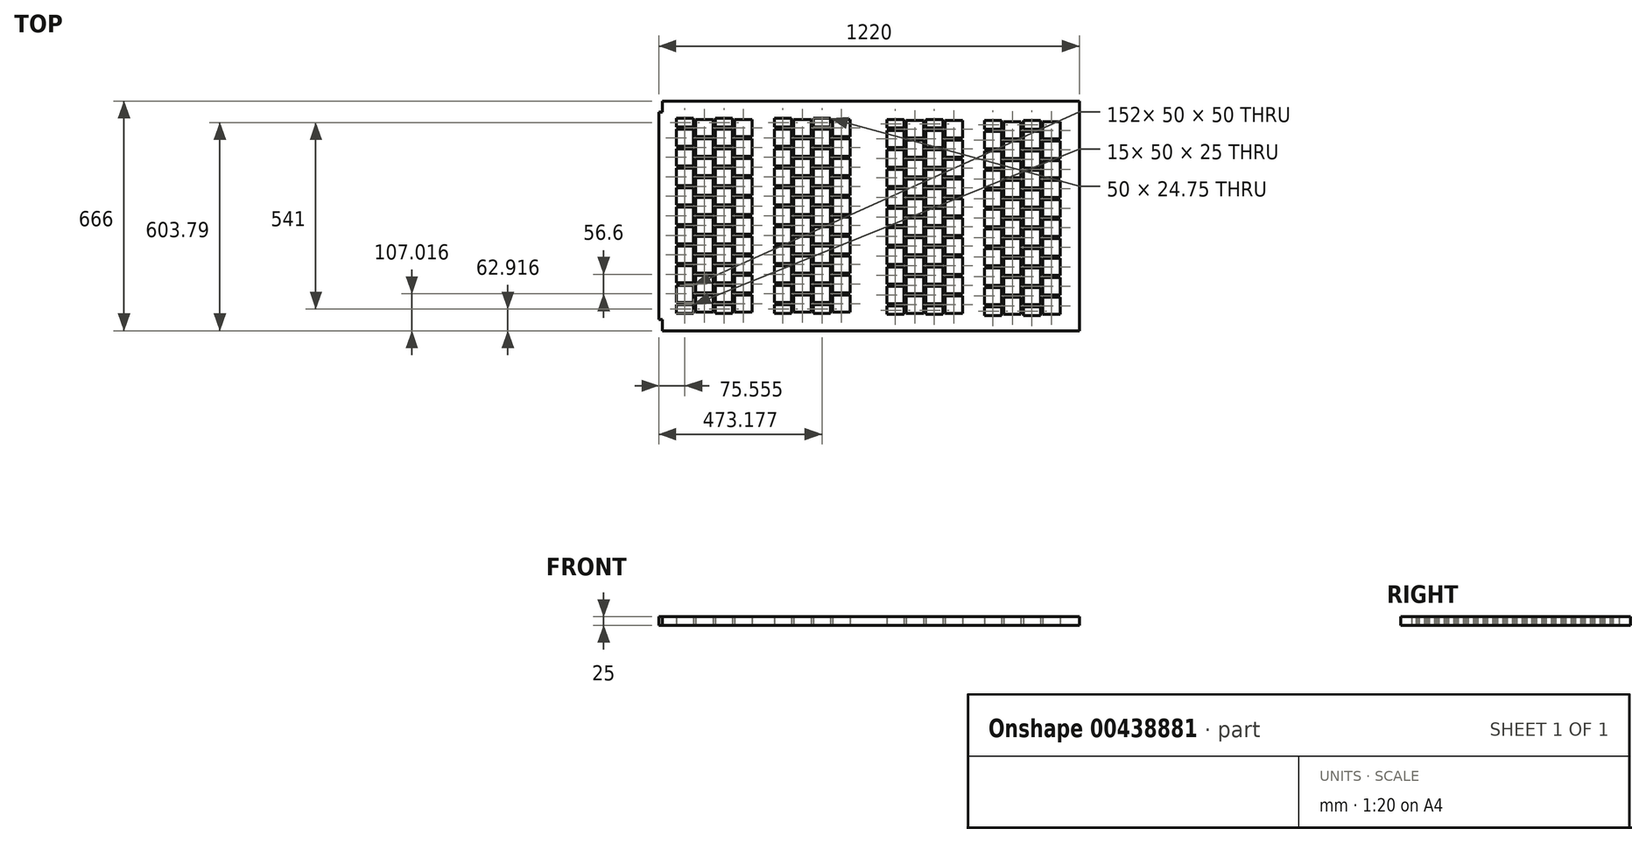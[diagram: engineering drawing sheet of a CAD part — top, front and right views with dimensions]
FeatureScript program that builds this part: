
annotation { "Feature Type Name" : "Feature", "Feature Type Description" : "" }
export const myFeature = defineFeature(function(context is Context, id is Id, definition is map)
    precondition{}
    {
        {
            var Q0;
            Q0=qCreatedBy(makeId("Top.planeOp"),FACE);
            var sketch = newSketch(context, id + "F0", { "sketchPlane" : qUnion([Q0])});
            skLineSegment(sketch, "E0", {"start": v(-1823.33, -56.7) * mm, "end": v(-1823.33, -81.7) * mm});
            skLineSegment(sketch, "E1", {"start": v(-1823.33, -81.7) * mm, "end": v(-1773.33, -81.7) * mm});
            skLineSegment(sketch, "E2", {"start": v(-1773.33, -81.7) * mm, "end": v(-1773.33, -56.7) * mm});
            skLineSegment(sketch, "E3.bottom", {"start": v(-1823.33, -88.3) * mm, "end": v(-1823.33, -138.3) * mm});
            skLineSegment(sketch, "E3.top", {"start": v(-1773.33, -88.3) * mm, "end": v(-1773.33, -138.3) * mm});
            skLineSegment(sketch, "E3.left", {"start": v(-1823.33, -88.3) * mm, "end": v(-1773.33, -88.3) * mm});
            skLineSegment(sketch, "E3.right", {"start": v(-1823.33, -138.3) * mm, "end": v(-1773.33, -138.3) * mm});
            skLineSegment(sketch, "E4.bottom", {"start": v(-1823.33, -144.9) * mm, "end": v(-1823.33, -194.9) * mm});
            skLineSegment(sketch, "E4.top", {"start": v(-1773.33, -144.9) * mm, "end": v(-1773.33, -194.9) * mm});
            skLineSegment(sketch, "E4.left", {"start": v(-1823.33, -144.9) * mm, "end": v(-1773.33, -144.9) * mm});
            skLineSegment(sketch, "E4.right", {"start": v(-1823.33, -194.9) * mm, "end": v(-1773.33, -194.9) * mm});
            skLineSegment(sketch, "E5.bottom", {"start": v(-1823.33, -201.5) * mm, "end": v(-1823.33, -251.5) * mm});
            skLineSegment(sketch, "E5.top", {"start": v(-1773.33, -201.5) * mm, "end": v(-1773.33, -251.5) * mm});
            skLineSegment(sketch, "E5.left", {"start": v(-1823.33, -201.5) * mm, "end": v(-1773.33, -201.5) * mm});
            skLineSegment(sketch, "E5.right", {"start": v(-1823.33, -251.5) * mm, "end": v(-1773.33, -251.5) * mm});
            skLineSegment(sketch, "E6.bottom", {"start": v(-1823.33, -258.1) * mm, "end": v(-1823.33, -308.1) * mm});
            skLineSegment(sketch, "E6.top", {"start": v(-1773.33, -258.1) * mm, "end": v(-1773.33, -308.1) * mm});
            skLineSegment(sketch, "E6.left", {"start": v(-1823.33, -258.1) * mm, "end": v(-1773.33, -258.1) * mm});
            skLineSegment(sketch, "E6.right", {"start": v(-1823.33, -308.1) * mm, "end": v(-1773.33, -308.1) * mm});
            skLineSegment(sketch, "E7.bottom", {"start": v(-1823.33, -314.7) * mm, "end": v(-1823.33, -339.7) * mm});
            skLineSegment(sketch, "E7.top", {"start": v(-1773.33, -314.7) * mm, "end": v(-1773.33, -339.7) * mm});
            skLineSegment(sketch, "E7.left", {"start": v(-1823.33, -314.7) * mm, "end": v(-1773.33, -314.7) * mm});
            skLineSegment(sketch, "E7.right", {"start": v(-1823.33, -339.7) * mm, "end": v(-1773.33, -339.7) * mm});
            skLineSegment(sketch, "E8.bottom", {"start": v(-1766.73, -60) * mm, "end": v(-1766.73, -110) * mm});
            skLineSegment(sketch, "E8.top", {"start": v(-1716.73, -60) * mm, "end": v(-1716.73, -110) * mm});
            skLineSegment(sketch, "E8.left", {"start": v(-1766.73, -60) * mm, "end": v(-1716.73, -60) * mm});
            skLineSegment(sketch, "E8.right", {"start": v(-1766.73, -110) * mm, "end": v(-1716.73, -110) * mm});
            skLineSegment(sketch, "E9.bottom", {"start": v(-1766.73, -116.6) * mm, "end": v(-1766.73, -166.6) * mm});
            skLineSegment(sketch, "E9.top", {"start": v(-1716.73, -116.6) * mm, "end": v(-1716.73, -166.6) * mm});
            skLineSegment(sketch, "E9.left", {"start": v(-1766.73, -116.6) * mm, "end": v(-1716.73, -116.6) * mm});
            skLineSegment(sketch, "E9.right", {"start": v(-1766.73, -166.6) * mm, "end": v(-1716.73, -166.6) * mm});
            skLineSegment(sketch, "E10.bottom", {"start": v(-1766.73, -173.2) * mm, "end": v(-1766.73, -223.2) * mm});
            skLineSegment(sketch, "E10.top", {"start": v(-1716.73, -173.2) * mm, "end": v(-1716.73, -223.2) * mm});
            skLineSegment(sketch, "E10.left", {"start": v(-1766.73, -173.2) * mm, "end": v(-1716.73, -173.2) * mm});
            skLineSegment(sketch, "E10.right", {"start": v(-1766.73, -223.2) * mm, "end": v(-1716.73, -223.2) * mm});
            skLineSegment(sketch, "E11.bottom", {"start": v(-1766.73, -229.8) * mm, "end": v(-1766.73, -279.8) * mm});
            skLineSegment(sketch, "E11.top", {"start": v(-1716.73, -229.8) * mm, "end": v(-1716.73, -279.8) * mm});
            skLineSegment(sketch, "E11.left", {"start": v(-1766.73, -229.8) * mm, "end": v(-1716.73, -229.8) * mm});
            skLineSegment(sketch, "E11.right", {"start": v(-1766.73, -279.8) * mm, "end": v(-1716.73, -279.8) * mm});
            skLineSegment(sketch, "E12.bottom", {"start": v(-1766.73, -286.4) * mm, "end": v(-1766.73, -336.4) * mm});
            skLineSegment(sketch, "E12.top", {"start": v(-1716.73, -286.4) * mm, "end": v(-1716.73, -336.4) * mm});
            skLineSegment(sketch, "E12.left", {"start": v(-1766.73, -286.4) * mm, "end": v(-1716.73, -286.4) * mm});
            skLineSegment(sketch, "E12.right", {"start": v(-1766.73, -336.4) * mm, "end": v(-1716.73, -336.4) * mm});
            skLineSegment(sketch, "E13", {"start": v(-1710.13, -56.7) * mm, "end": v(-1710.13, -81.7) * mm});
            skLineSegment(sketch, "E14", {"start": v(-1710.13, -81.7) * mm, "end": v(-1660.13, -81.7) * mm});
            skLineSegment(sketch, "E15", {"start": v(-1660.13, -81.7) * mm, "end": v(-1660.13, -56.7) * mm});
            skLineSegment(sketch, "E16.bottom", {"start": v(-1710.13, -88.3) * mm, "end": v(-1710.13, -138.3) * mm});
            skLineSegment(sketch, "E16.top", {"start": v(-1660.13, -88.3) * mm, "end": v(-1660.13, -138.3) * mm});
            skLineSegment(sketch, "E16.left", {"start": v(-1710.13, -88.3) * mm, "end": v(-1660.13, -88.3) * mm});
            skLineSegment(sketch, "E16.right", {"start": v(-1710.13, -138.3) * mm, "end": v(-1660.13, -138.3) * mm});
            skLineSegment(sketch, "E17.bottom", {"start": v(-1710.13, -144.9) * mm, "end": v(-1710.13, -194.9) * mm});
            skLineSegment(sketch, "E17.top", {"start": v(-1660.13, -144.9) * mm, "end": v(-1660.13, -194.9) * mm});
            skLineSegment(sketch, "E17.left", {"start": v(-1710.13, -144.9) * mm, "end": v(-1660.13, -144.9) * mm});
            skLineSegment(sketch, "E17.right", {"start": v(-1710.13, -194.9) * mm, "end": v(-1660.13, -194.9) * mm});
            skLineSegment(sketch, "E18.bottom", {"start": v(-1710.13, -201.5) * mm, "end": v(-1710.13, -251.5) * mm});
            skLineSegment(sketch, "E18.top", {"start": v(-1660.13, -201.5) * mm, "end": v(-1660.13, -251.5) * mm});
            skLineSegment(sketch, "E18.left", {"start": v(-1710.13, -201.5) * mm, "end": v(-1660.13, -201.5) * mm});
            skLineSegment(sketch, "E18.right", {"start": v(-1710.13, -251.5) * mm, "end": v(-1660.13, -251.5) * mm});
            skLineSegment(sketch, "E19.bottom", {"start": v(-1710.13, -258.1) * mm, "end": v(-1710.13, -308.1) * mm});
            skLineSegment(sketch, "E19.top", {"start": v(-1660.13, -258.1) * mm, "end": v(-1660.13, -308.1) * mm});
            skLineSegment(sketch, "E19.left", {"start": v(-1710.13, -258.1) * mm, "end": v(-1660.13, -258.1) * mm});
            skLineSegment(sketch, "E19.right", {"start": v(-1710.13, -308.1) * mm, "end": v(-1660.13, -308.1) * mm});
            skLineSegment(sketch, "E20.bottom", {"start": v(-1710.13, -314.7) * mm, "end": v(-1710.13, -339.7) * mm});
            skLineSegment(sketch, "E20.top", {"start": v(-1660.13, -314.7) * mm, "end": v(-1660.13, -339.7) * mm});
            skLineSegment(sketch, "E20.left", {"start": v(-1710.13, -314.7) * mm, "end": v(-1660.13, -314.7) * mm});
            skLineSegment(sketch, "E20.right", {"start": v(-1710.13, -339.7) * mm, "end": v(-1660.13, -339.7) * mm});
            skLineSegment(sketch, "E21.bottom", {"start": v(-1653.53, -60) * mm, "end": v(-1653.53, -110) * mm});
            skLineSegment(sketch, "E21.top", {"start": v(-1603.53, -60) * mm, "end": v(-1603.53, -110) * mm});
            skLineSegment(sketch, "E21.left", {"start": v(-1653.53, -60) * mm, "end": v(-1603.53, -60) * mm});
            skLineSegment(sketch, "E21.right", {"start": v(-1653.53, -110) * mm, "end": v(-1603.53, -110) * mm});
            skLineSegment(sketch, "E22.bottom", {"start": v(-1653.53, -116.6) * mm, "end": v(-1653.53, -166.6) * mm});
            skLineSegment(sketch, "E22.top", {"start": v(-1603.53, -116.6) * mm, "end": v(-1603.53, -166.6) * mm});
            skLineSegment(sketch, "E22.left", {"start": v(-1653.53, -116.6) * mm, "end": v(-1603.53, -116.6) * mm});
            skLineSegment(sketch, "E22.right", {"start": v(-1653.53, -166.6) * mm, "end": v(-1603.53, -166.6) * mm});
            skLineSegment(sketch, "E23.bottom", {"start": v(-1653.53, -173.2) * mm, "end": v(-1653.53, -223.2) * mm});
            skLineSegment(sketch, "E23.top", {"start": v(-1603.53, -173.2) * mm, "end": v(-1603.53, -223.2) * mm});
            skLineSegment(sketch, "E23.left", {"start": v(-1653.53, -173.2) * mm, "end": v(-1603.53, -173.2) * mm});
            skLineSegment(sketch, "E23.right", {"start": v(-1653.53, -223.2) * mm, "end": v(-1603.53, -223.2) * mm});
            skLineSegment(sketch, "E24.bottom", {"start": v(-1653.53, -229.8) * mm, "end": v(-1653.53, -279.8) * mm});
            skLineSegment(sketch, "E24.top", {"start": v(-1603.53, -229.8) * mm, "end": v(-1603.53, -279.8) * mm});
            skLineSegment(sketch, "E24.left", {"start": v(-1653.53, -229.8) * mm, "end": v(-1603.53, -229.8) * mm});
            skLineSegment(sketch, "E24.right", {"start": v(-1653.53, -279.8) * mm, "end": v(-1603.53, -279.8) * mm});
            skLineSegment(sketch, "E25.bottom", {"start": v(-1653.53, -286.4) * mm, "end": v(-1653.53, -336.4) * mm});
            skLineSegment(sketch, "E25.top", {"start": v(-1603.53, -286.4) * mm, "end": v(-1603.53, -336.4) * mm});
            skLineSegment(sketch, "E25.left", {"start": v(-1653.53, -286.4) * mm, "end": v(-1603.53, -286.4) * mm});
            skLineSegment(sketch, "E25.right", {"start": v(-1653.53, -336.4) * mm, "end": v(-1603.53, -336.4) * mm});
            skLineSegment(sketch, "E26.MirrorCS", {"start": v(-1710.13, 201.3) * mm, "end": v(-1660.13, 201.3) * mm});
            skLineSegment(sketch, "E27.MirrorCS", {"start": v(-1653.53, 116.4) * mm, "end": v(-1603.53, 116.4) * mm});
            skLineSegment(sketch, "E28.MirrorCS", {"start": v(-1823.33, 144.7) * mm, "end": v(-1773.33, 144.7) * mm});
            skLineSegment(sketch, "E29.MirrorCS", {"start": v(-1603.53, 3.2) * mm, "end": v(-1603.53, 53.2) * mm});
            skLineSegment(sketch, "E30.MirrorCS", {"start": v(-1716.73, -53.4) * mm, "end": v(-1716.73, -3.4) * mm});
            skLineSegment(sketch, "E31.MirrorCS", {"start": v(-1716.73, 173) * mm, "end": v(-1716.73, 223) * mm});
            skLineSegment(sketch, "E32.MirrorCS", {"start": v(-1660.13, 88.1) * mm, "end": v(-1660.13, 138.1) * mm});
            skLineSegment(sketch, "E33.MirrorCS", {"start": v(-1716.73, 59.8) * mm, "end": v(-1716.73, 109.8) * mm});
            skLineSegment(sketch, "E34.MirrorCS", {"start": v(-1660.13, -25.1) * mm, "end": v(-1660.13, 24.9) * mm});
            skLineSegment(sketch, "E35.MirrorCS", {"start": v(-1660.13, 201.3) * mm, "end": v(-1660.13, 226.3) * mm});
            skLineSegment(sketch, "E36.MirrorCS", {"start": v(-1603.53, 116.4) * mm, "end": v(-1603.53, 166.4) * mm});
            skLineSegment(sketch, "E37.MirrorCS", {"start": v(-1773.33, 144.7) * mm, "end": v(-1773.33, 194.7) * mm});
            skLineSegment(sketch, "E38.MirrorCS", {"start": v(-1653.53, 3.2) * mm, "end": v(-1653.53, 53.2) * mm});
            skLineSegment(sketch, "E39.MirrorCS", {"start": v(-1766.73, 59.8) * mm, "end": v(-1716.73, 59.8) * mm});
            skLineSegment(sketch, "E40.MirrorCS", {"start": v(-1766.73, -53.4) * mm, "end": v(-1766.73, -3.4) * mm});
            skLineSegment(sketch, "E41.MirrorCS", {"start": v(-1766.73, 173) * mm, "end": v(-1766.73, 223) * mm});
            skLineSegment(sketch, "E42.MirrorCS", {"start": v(-1710.13, 88.1) * mm, "end": v(-1710.13, 138.1) * mm});
            skLineSegment(sketch, "E43.MirrorCS", {"start": v(-1766.73, 59.8) * mm, "end": v(-1766.73, 109.8) * mm});
            skLineSegment(sketch, "E44.MirrorCS", {"start": v(-1710.13, -25.1) * mm, "end": v(-1710.13, 24.9) * mm});
            skLineSegment(sketch, "E45.MirrorCS", {"start": v(-1710.13, 201.3) * mm, "end": v(-1710.13, 226.3) * mm});
            skLineSegment(sketch, "E46.MirrorCS", {"start": v(-1653.53, 116.4) * mm, "end": v(-1653.53, 166.4) * mm});
            skLineSegment(sketch, "E47.MirrorCS", {"start": v(-1823.33, 144.7) * mm, "end": v(-1823.33, 194.7) * mm});
            skLineSegment(sketch, "E48.MirrorCS", {"start": v(-1653.53, -3.4) * mm, "end": v(-1603.53, -3.4) * mm});
            skLineSegment(sketch, "E49.MirrorCS", {"start": v(-1653.53, 223) * mm, "end": v(-1603.53, 223) * mm});
            skLineSegment(sketch, "E50.MirrorCS", {"start": v(-1823.33, 226.3) * mm, "end": v(-1773.33, 226.3) * mm});
            skLineSegment(sketch, "E51.MirrorCS", {"start": v(-1766.73, 166.4) * mm, "end": v(-1716.73, 166.4) * mm});
            skLineSegment(sketch, "E52.MirrorCS", {"start": v(-1710.13, 81.5) * mm, "end": v(-1660.13, 81.5) * mm});
            skLineSegment(sketch, "E53.MirrorCS", {"start": v(-1823.33, 88.1) * mm, "end": v(-1823.33, 138.1) * mm});
            skLineSegment(sketch, "E54.MirrorCS", {"start": v(-1823.33, 81.5) * mm, "end": v(-1773.33, 81.5) * mm});
            skLineSegment(sketch, "E55.MirrorCS", {"start": v(-1823.33, 31.5) * mm, "end": v(-1773.33, 31.5) * mm});
            skLineSegment(sketch, "E56.MirrorCS", {"start": v(-1773.33, 31.5) * mm, "end": v(-1773.33, 81.5) * mm});
            skLineSegment(sketch, "E57.MirrorCS", {"start": v(-1823.33, 31.5) * mm, "end": v(-1823.33, 81.5) * mm});
            skLineSegment(sketch, "E58.MirrorCS", {"start": v(-1823.33, 24.9) * mm, "end": v(-1773.33, 24.9) * mm});
            skLineSegment(sketch, "E59.MirrorCS", {"start": v(-1823.33, -25.1) * mm, "end": v(-1773.33, -25.1) * mm});
            skLineSegment(sketch, "E60.MirrorCS", {"start": v(-1773.33, -25.1) * mm, "end": v(-1773.33, 24.9) * mm});
            skLineSegment(sketch, "E61.MirrorCS", {"start": v(-1823.33, -25.1) * mm, "end": v(-1823.33, 24.9) * mm});
            skLineSegment(sketch, "E62.MirrorCS", {"start": v(-1773.33, -31.7) * mm, "end": v(-1773.33, -56.7) * mm});
            skLineSegment(sketch, "E63.MirrorCS", {"start": v(-1823.33, -31.7) * mm, "end": v(-1773.33, -31.7) * mm});
            skLineSegment(sketch, "E64.MirrorCS", {"start": v(-1823.33, -56.7) * mm, "end": v(-1823.33, -31.7) * mm});
            skLineSegment(sketch, "E65.MirrorCS", {"start": v(-1823.33, 138.1) * mm, "end": v(-1773.33, 138.1) * mm});
            skLineSegment(sketch, "E66.MirrorCS", {"start": v(-1823.33, 88.1) * mm, "end": v(-1773.33, 88.1) * mm});
            skLineSegment(sketch, "E67.MirrorCS", {"start": v(-1710.13, -25.1) * mm, "end": v(-1660.13, -25.1) * mm});
            skLineSegment(sketch, "E68.MirrorCS", {"start": v(-1773.33, 88.1) * mm, "end": v(-1773.33, 138.1) * mm});
            skLineSegment(sketch, "E69.MirrorCS", {"start": v(-1766.73, 116.4) * mm, "end": v(-1716.73, 116.4) * mm});
            skLineSegment(sketch, "E70.MirrorCS", {"start": v(-1766.73, 53.2) * mm, "end": v(-1716.73, 53.2) * mm});
            skLineSegment(sketch, "E71.MirrorCS", {"start": v(-1710.13, 31.5) * mm, "end": v(-1660.13, 31.5) * mm});
            skLineSegment(sketch, "E72.MirrorCS", {"start": v(-1660.13, -31.7) * mm, "end": v(-1660.13, -56.7) * mm});
            skLineSegment(sketch, "E73.MirrorCS", {"start": v(-1710.13, 194.7) * mm, "end": v(-1660.13, 194.7) * mm});
            skLineSegment(sketch, "E74.MirrorCS", {"start": v(-1653.53, -53.4) * mm, "end": v(-1603.53, -53.4) * mm});
            skLineSegment(sketch, "E75.MirrorCS", {"start": v(-1653.53, 173) * mm, "end": v(-1603.53, 173) * mm});
            skLineSegment(sketch, "E76.MirrorCS", {"start": v(-1653.53, 109.8) * mm, "end": v(-1603.53, 109.8) * mm});
            skLineSegment(sketch, "E77.MirrorCS", {"start": v(-1823.33, 201.3) * mm, "end": v(-1773.33, 201.3) * mm});
            skLineSegment(sketch, "E78.MirrorCS", {"start": v(-1766.73, 116.4) * mm, "end": v(-1766.73, 166.4) * mm});
            skLineSegment(sketch, "E79.MirrorCS", {"start": v(-1716.73, 3.2) * mm, "end": v(-1716.73, 53.2) * mm});
            skLineSegment(sketch, "E80.MirrorCS", {"start": v(-1710.13, 31.5) * mm, "end": v(-1710.13, 81.5) * mm});
            skLineSegment(sketch, "E81.MirrorCS", {"start": v(-1710.13, 88.1) * mm, "end": v(-1660.13, 88.1) * mm});
            skLineSegment(sketch, "E82.MirrorCS", {"start": v(-1766.73, 173) * mm, "end": v(-1716.73, 173) * mm});
            skLineSegment(sketch, "E83.MirrorCS", {"start": v(-1766.73, 223) * mm, "end": v(-1716.73, 223) * mm});
            skLineSegment(sketch, "E84.MirrorCS", {"start": v(-1710.13, 138.1) * mm, "end": v(-1660.13, 138.1) * mm});
            skLineSegment(sketch, "E85.MirrorCS", {"start": v(-1823.33, 201.3) * mm, "end": v(-1823.33, 226.3) * mm});
            skLineSegment(sketch, "E86.MirrorCS", {"start": v(-1766.73, -53.4) * mm, "end": v(-1716.73, -53.4) * mm});
            skLineSegment(sketch, "E87.MirrorCS", {"start": v(-1716.73, 116.4) * mm, "end": v(-1716.73, 166.4) * mm});
            skLineSegment(sketch, "E88.MirrorCS", {"start": v(-1766.73, 3.2) * mm, "end": v(-1716.73, 3.2) * mm});
            skLineSegment(sketch, "E89.MirrorCS", {"start": v(-1766.73, -3.4) * mm, "end": v(-1716.73, -3.4) * mm});
            skLineSegment(sketch, "E90.MirrorCS", {"start": v(-1653.53, 53.2) * mm, "end": v(-1603.53, 53.2) * mm});
            skLineSegment(sketch, "E91.MirrorCS", {"start": v(-1653.53, 173) * mm, "end": v(-1653.53, 223) * mm});
            skLineSegment(sketch, "E92.MirrorCS", {"start": v(-1603.53, 59.8) * mm, "end": v(-1603.53, 109.8) * mm});
            skLineSegment(sketch, "E93.MirrorCS", {"start": v(-1823.33, 194.7) * mm, "end": v(-1773.33, 194.7) * mm});
            skLineSegment(sketch, "E94.MirrorCS", {"start": v(-1653.53, 166.4) * mm, "end": v(-1603.53, 166.4) * mm});
            skLineSegment(sketch, "E95.MirrorCS", {"start": v(-1766.73, 3.2) * mm, "end": v(-1766.73, 53.2) * mm});
            skLineSegment(sketch, "E96.MirrorCS", {"start": v(-1710.13, 226.3) * mm, "end": v(-1660.13, 226.3) * mm});
            skLineSegment(sketch, "E97.MirrorCS", {"start": v(-1710.13, 144.7) * mm, "end": v(-1710.13, 194.7) * mm});
            skLineSegment(sketch, "E98.MirrorCS", {"start": v(-1653.53, 59.8) * mm, "end": v(-1653.53, 109.8) * mm});
            skLineSegment(sketch, "E99.MirrorCS", {"start": v(-1710.13, -56.7) * mm, "end": v(-1710.13, -31.7) * mm});
            skLineSegment(sketch, "E100.MirrorCS", {"start": v(-1710.13, -31.7) * mm, "end": v(-1660.13, -31.7) * mm});
            skLineSegment(sketch, "E101.MirrorCS", {"start": v(-1660.13, 144.7) * mm, "end": v(-1660.13, 194.7) * mm});
            skLineSegment(sketch, "E102.MirrorCS", {"start": v(-1660.13, 31.5) * mm, "end": v(-1660.13, 81.5) * mm});
            skLineSegment(sketch, "E103.MirrorCS", {"start": v(-1603.53, -53.4) * mm, "end": v(-1603.53, -3.4) * mm});
            skLineSegment(sketch, "E104.MirrorCS", {"start": v(-1766.73, 109.8) * mm, "end": v(-1716.73, 109.8) * mm});
            skLineSegment(sketch, "E105.MirrorCS", {"start": v(-1710.13, 24.9) * mm, "end": v(-1660.13, 24.9) * mm});
            skLineSegment(sketch, "E106.MirrorCS", {"start": v(-1773.33, 201.3) * mm, "end": v(-1773.33, 226.3) * mm});
            skLineSegment(sketch, "E107.MirrorCS", {"start": v(-1653.53, 3.2) * mm, "end": v(-1603.53, 3.2) * mm});
            skLineSegment(sketch, "E108.MirrorCS", {"start": v(-1653.53, 59.8) * mm, "end": v(-1603.53, 59.8) * mm});
            skLineSegment(sketch, "E109.MirrorCS", {"start": v(-1603.53, 173) * mm, "end": v(-1603.53, 223) * mm});
            skLineSegment(sketch, "E110.MirrorCS", {"start": v(-1653.53, -53.4) * mm, "end": v(-1653.53, -3.4) * mm});
            skLineSegment(sketch, "E111.MirrorCS", {"start": v(-1710.13, 144.7) * mm, "end": v(-1660.13, 144.7) * mm});
            skPoint(sketch, "E112.MirrorCS.end.orphan", {"position": v(-1650.16, -56.7) * mm});
            skLineSegment(sketch, "E113", {"start": v(-1538.9, -56.7) * mm, "end": v(-1538.9, -81.7) * mm});
            skLineSegment(sketch, "E114", {"start": v(-1538.9, -81.7) * mm, "end": v(-1488.9, -81.7) * mm});
            skLineSegment(sketch, "E115", {"start": v(-1488.9, -81.7) * mm, "end": v(-1488.9, -56.7) * mm});
            skLineSegment(sketch, "E116.bottom", {"start": v(-1538.9, -88.3) * mm, "end": v(-1538.9, -138.3) * mm});
            skLineSegment(sketch, "E116.top", {"start": v(-1488.9, -88.3) * mm, "end": v(-1488.9, -138.3) * mm});
            skLineSegment(sketch, "E116.left", {"start": v(-1538.9, -88.3) * mm, "end": v(-1488.9, -88.3) * mm});
            skLineSegment(sketch, "E116.right", {"start": v(-1538.9, -138.3) * mm, "end": v(-1488.9, -138.3) * mm});
            skLineSegment(sketch, "E117.bottom", {"start": v(-1538.9, -144.9) * mm, "end": v(-1538.9, -194.9) * mm});
            skLineSegment(sketch, "E117.top", {"start": v(-1488.9, -144.9) * mm, "end": v(-1488.9, -194.9) * mm});
            skLineSegment(sketch, "E117.left", {"start": v(-1538.9, -144.9) * mm, "end": v(-1488.9, -144.9) * mm});
            skLineSegment(sketch, "E117.right", {"start": v(-1538.9, -194.9) * mm, "end": v(-1488.9, -194.9) * mm});
            skLineSegment(sketch, "E118.bottom", {"start": v(-1538.9, -201.5) * mm, "end": v(-1538.9, -251.5) * mm});
            skLineSegment(sketch, "E118.top", {"start": v(-1488.9, -201.5) * mm, "end": v(-1488.9, -251.5) * mm});
            skLineSegment(sketch, "E118.left", {"start": v(-1538.9, -201.5) * mm, "end": v(-1488.9, -201.5) * mm});
            skLineSegment(sketch, "E118.right", {"start": v(-1538.9, -251.5) * mm, "end": v(-1488.9, -251.5) * mm});
            skLineSegment(sketch, "E119.bottom", {"start": v(-1538.9, -258.1) * mm, "end": v(-1538.9, -308.1) * mm});
            skLineSegment(sketch, "E119.top", {"start": v(-1488.9, -258.1) * mm, "end": v(-1488.9, -308.1) * mm});
            skLineSegment(sketch, "E119.left", {"start": v(-1538.9, -258.1) * mm, "end": v(-1488.9, -258.1) * mm});
            skLineSegment(sketch, "E119.right", {"start": v(-1538.9, -308.1) * mm, "end": v(-1488.9, -308.1) * mm});
            skLineSegment(sketch, "E120.bottom", {"start": v(-1538.9, -314.7) * mm, "end": v(-1538.9, -339.7) * mm});
            skLineSegment(sketch, "E120.top", {"start": v(-1488.9, -314.7) * mm, "end": v(-1488.9, -339.7) * mm});
            skLineSegment(sketch, "E120.left", {"start": v(-1538.9, -314.7) * mm, "end": v(-1488.9, -314.7) * mm});
            skLineSegment(sketch, "E120.right", {"start": v(-1538.9, -339.7) * mm, "end": v(-1488.9, -339.7) * mm});
            skLineSegment(sketch, "E121.bottom", {"start": v(-1482.3, -60) * mm, "end": v(-1482.3, -110) * mm});
            skLineSegment(sketch, "E121.top", {"start": v(-1432.3, -60) * mm, "end": v(-1432.3, -110) * mm});
            skLineSegment(sketch, "E121.left", {"start": v(-1482.3, -60) * mm, "end": v(-1432.3, -60) * mm});
            skLineSegment(sketch, "E121.right", {"start": v(-1482.3, -110) * mm, "end": v(-1432.3, -110) * mm});
            skLineSegment(sketch, "E122.bottom", {"start": v(-1482.3, -116.6) * mm, "end": v(-1482.3, -166.6) * mm});
            skLineSegment(sketch, "E122.top", {"start": v(-1432.3, -116.6) * mm, "end": v(-1432.3, -166.6) * mm});
            skLineSegment(sketch, "E122.left", {"start": v(-1482.3, -116.6) * mm, "end": v(-1432.3, -116.6) * mm});
            skLineSegment(sketch, "E122.right", {"start": v(-1482.3, -166.6) * mm, "end": v(-1432.3, -166.6) * mm});
            skLineSegment(sketch, "E123.bottom", {"start": v(-1482.3, -173.2) * mm, "end": v(-1482.3, -223.2) * mm});
            skLineSegment(sketch, "E123.top", {"start": v(-1432.3, -173.2) * mm, "end": v(-1432.3, -223.2) * mm});
            skLineSegment(sketch, "E123.left", {"start": v(-1482.3, -173.2) * mm, "end": v(-1432.3, -173.2) * mm});
            skLineSegment(sketch, "E123.right", {"start": v(-1482.3, -223.2) * mm, "end": v(-1432.3, -223.2) * mm});
            skLineSegment(sketch, "E124.bottom", {"start": v(-1482.3, -229.8) * mm, "end": v(-1482.3, -279.8) * mm});
            skLineSegment(sketch, "E124.top", {"start": v(-1432.3, -229.8) * mm, "end": v(-1432.3, -279.8) * mm});
            skLineSegment(sketch, "E124.left", {"start": v(-1482.3, -229.8) * mm, "end": v(-1432.3, -229.8) * mm});
            skLineSegment(sketch, "E124.right", {"start": v(-1482.3, -279.8) * mm, "end": v(-1432.3, -279.8) * mm});
            skLineSegment(sketch, "E125.bottom", {"start": v(-1482.3, -286.4) * mm, "end": v(-1482.3, -336.4) * mm});
            skLineSegment(sketch, "E125.top", {"start": v(-1432.3, -286.4) * mm, "end": v(-1432.3, -336.4) * mm});
            skLineSegment(sketch, "E125.left", {"start": v(-1482.3, -286.4) * mm, "end": v(-1432.3, -286.4) * mm});
            skLineSegment(sketch, "E125.right", {"start": v(-1482.3, -336.4) * mm, "end": v(-1432.3, -336.4) * mm});
            skLineSegment(sketch, "E126", {"start": v(-1425.7, -56.7) * mm, "end": v(-1425.7, -81.7) * mm});
            skLineSegment(sketch, "E127", {"start": v(-1425.7, -81.7) * mm, "end": v(-1375.7, -81.7) * mm});
            skLineSegment(sketch, "E128", {"start": v(-1375.7, -81.7) * mm, "end": v(-1375.7, -56.7) * mm});
            skLineSegment(sketch, "E129.bottom", {"start": v(-1425.7, -88.3) * mm, "end": v(-1425.7, -138.3) * mm});
            skLineSegment(sketch, "E129.top", {"start": v(-1375.7, -88.3) * mm, "end": v(-1375.7, -138.3) * mm});
            skLineSegment(sketch, "E129.left", {"start": v(-1425.7, -88.3) * mm, "end": v(-1375.7, -88.3) * mm});
            skLineSegment(sketch, "E129.right", {"start": v(-1425.7, -138.3) * mm, "end": v(-1375.7, -138.3) * mm});
            skLineSegment(sketch, "E130.bottom", {"start": v(-1425.7, -144.9) * mm, "end": v(-1425.7, -194.9) * mm});
            skLineSegment(sketch, "E130.top", {"start": v(-1375.7, -144.9) * mm, "end": v(-1375.7, -194.9) * mm});
            skLineSegment(sketch, "E130.left", {"start": v(-1425.7, -144.9) * mm, "end": v(-1375.7, -144.9) * mm});
            skLineSegment(sketch, "E130.right", {"start": v(-1425.7, -194.9) * mm, "end": v(-1375.7, -194.9) * mm});
            skLineSegment(sketch, "E131.bottom", {"start": v(-1425.7, -201.5) * mm, "end": v(-1425.7, -251.5) * mm});
            skLineSegment(sketch, "E131.top", {"start": v(-1375.7, -201.5) * mm, "end": v(-1375.7, -251.5) * mm});
            skLineSegment(sketch, "E131.left", {"start": v(-1425.7, -201.5) * mm, "end": v(-1375.7, -201.5) * mm});
            skLineSegment(sketch, "E131.right", {"start": v(-1425.7, -251.5) * mm, "end": v(-1375.7, -251.5) * mm});
            skLineSegment(sketch, "E132.bottom", {"start": v(-1425.7, -258.1) * mm, "end": v(-1425.7, -308.1) * mm});
            skLineSegment(sketch, "E132.top", {"start": v(-1375.7, -258.1) * mm, "end": v(-1375.7, -308.1) * mm});
            skLineSegment(sketch, "E132.left", {"start": v(-1425.7, -258.1) * mm, "end": v(-1375.7, -258.1) * mm});
            skLineSegment(sketch, "E132.right", {"start": v(-1425.7, -308.1) * mm, "end": v(-1375.7, -308.1) * mm});
            skLineSegment(sketch, "E133.bottom", {"start": v(-1425.7, -314.7) * mm, "end": v(-1425.7, -339.7) * mm});
            skLineSegment(sketch, "E133.top", {"start": v(-1375.7, -314.7) * mm, "end": v(-1375.7, -339.7) * mm});
            skLineSegment(sketch, "E133.left", {"start": v(-1425.7, -314.7) * mm, "end": v(-1375.7, -314.7) * mm});
            skLineSegment(sketch, "E133.right", {"start": v(-1425.7, -339.7) * mm, "end": v(-1375.7, -339.7) * mm});
            skLineSegment(sketch, "E134.bottom", {"start": v(-1369.1, -60) * mm, "end": v(-1369.1, -110) * mm});
            skLineSegment(sketch, "E134.top", {"start": v(-1319.1, -60) * mm, "end": v(-1319.1, -110) * mm});
            skLineSegment(sketch, "E134.left", {"start": v(-1369.1, -60) * mm, "end": v(-1319.1, -60) * mm});
            skLineSegment(sketch, "E134.right", {"start": v(-1369.1, -110) * mm, "end": v(-1319.1, -110) * mm});
            skLineSegment(sketch, "E135.bottom", {"start": v(-1369.1, -116.6) * mm, "end": v(-1369.1, -166.6) * mm});
            skLineSegment(sketch, "E135.top", {"start": v(-1319.1, -116.6) * mm, "end": v(-1319.1, -166.6) * mm});
            skLineSegment(sketch, "E135.left", {"start": v(-1369.1, -116.6) * mm, "end": v(-1319.1, -116.6) * mm});
            skLineSegment(sketch, "E135.right", {"start": v(-1369.1, -166.6) * mm, "end": v(-1319.1, -166.6) * mm});
            skLineSegment(sketch, "E136.bottom", {"start": v(-1369.1, -173.2) * mm, "end": v(-1369.1, -223.2) * mm});
            skLineSegment(sketch, "E136.top", {"start": v(-1319.1, -173.2) * mm, "end": v(-1319.1, -223.2) * mm});
            skLineSegment(sketch, "E136.left", {"start": v(-1369.1, -173.2) * mm, "end": v(-1319.1, -173.2) * mm});
            skLineSegment(sketch, "E136.right", {"start": v(-1369.1, -223.2) * mm, "end": v(-1319.1, -223.2) * mm});
            skLineSegment(sketch, "E137.bottom", {"start": v(-1369.1, -229.8) * mm, "end": v(-1369.1, -279.8) * mm});
            skLineSegment(sketch, "E137.top", {"start": v(-1319.1, -229.8) * mm, "end": v(-1319.1, -279.8) * mm});
            skLineSegment(sketch, "E137.left", {"start": v(-1369.1, -229.8) * mm, "end": v(-1319.1, -229.8) * mm});
            skLineSegment(sketch, "E137.right", {"start": v(-1369.1, -279.8) * mm, "end": v(-1319.1, -279.8) * mm});
            skLineSegment(sketch, "E138.bottom", {"start": v(-1369.1, -286.4) * mm, "end": v(-1369.1, -336.4) * mm});
            skLineSegment(sketch, "E138.top", {"start": v(-1319.1, -286.4) * mm, "end": v(-1319.1, -336.4) * mm});
            skLineSegment(sketch, "E138.left", {"start": v(-1369.1, -286.4) * mm, "end": v(-1319.1, -286.4) * mm});
            skLineSegment(sketch, "E138.right", {"start": v(-1369.1, -336.4) * mm, "end": v(-1319.1, -336.4) * mm});
            skLineSegment(sketch, "E139.MirrorCS", {"start": v(-1425.7, 201.3) * mm, "end": v(-1375.7, 201.3) * mm});
            skLineSegment(sketch, "E140.MirrorCS", {"start": v(-1369.1, 116.4) * mm, "end": v(-1319.1, 116.4) * mm});
            skLineSegment(sketch, "E141.MirrorCS", {"start": v(-1538.9, 144.7) * mm, "end": v(-1488.9, 144.7) * mm});
            skLineSegment(sketch, "E142.MirrorCS", {"start": v(-1319.1, 3.2) * mm, "end": v(-1319.1, 53.2) * mm});
            skLineSegment(sketch, "E143.MirrorCS", {"start": v(-1432.3, -53.4) * mm, "end": v(-1432.3, -3.4) * mm});
            skLineSegment(sketch, "E144.MirrorCS", {"start": v(-1432.3, 173) * mm, "end": v(-1432.3, 223) * mm});
            skLineSegment(sketch, "E145.MirrorCS", {"start": v(-1375.7, 88.1) * mm, "end": v(-1375.7, 138.1) * mm});
            skLineSegment(sketch, "E146.MirrorCS", {"start": v(-1432.3, 59.8) * mm, "end": v(-1432.3, 109.8) * mm});
            skLineSegment(sketch, "E147.MirrorCS", {"start": v(-1375.7, -25.1) * mm, "end": v(-1375.7, 24.9) * mm});
            skLineSegment(sketch, "E148.MirrorCS", {"start": v(-1375.7, 201.3) * mm, "end": v(-1375.7, 226.3) * mm});
            skLineSegment(sketch, "E149.MirrorCS", {"start": v(-1319.1, 116.4) * mm, "end": v(-1319.1, 166.4) * mm});
            skLineSegment(sketch, "E150.MirrorCS", {"start": v(-1488.9, 144.7) * mm, "end": v(-1488.9, 194.7) * mm});
            skLineSegment(sketch, "E151.MirrorCS", {"start": v(-1369.1, 3.2) * mm, "end": v(-1369.1, 53.2) * mm});
            skLineSegment(sketch, "E152.MirrorCS", {"start": v(-1482.3, 59.8) * mm, "end": v(-1432.3, 59.8) * mm});
            skLineSegment(sketch, "E153.MirrorCS", {"start": v(-1482.3, -53.4) * mm, "end": v(-1482.3, -3.4) * mm});
            skLineSegment(sketch, "E154.MirrorCS", {"start": v(-1482.3, 173) * mm, "end": v(-1482.3, 223) * mm});
            skLineSegment(sketch, "E155.MirrorCS", {"start": v(-1425.7, 88.1) * mm, "end": v(-1425.7, 138.1) * mm});
            skLineSegment(sketch, "E156.MirrorCS", {"start": v(-1482.3, 59.8) * mm, "end": v(-1482.3, 109.8) * mm});
            skLineSegment(sketch, "E157.MirrorCS", {"start": v(-1425.7, -25.1) * mm, "end": v(-1425.7, 24.9) * mm});
            skLineSegment(sketch, "E158.MirrorCS", {"start": v(-1425.7, 201.3) * mm, "end": v(-1425.7, 226.3) * mm});
            skLineSegment(sketch, "E159.MirrorCS", {"start": v(-1369.1, 116.4) * mm, "end": v(-1369.1, 166.4) * mm});
            skLineSegment(sketch, "E160.MirrorCS", {"start": v(-1538.9, 144.7) * mm, "end": v(-1538.9, 194.7) * mm});
            skLineSegment(sketch, "E161.MirrorCS", {"start": v(-1369.1, -3.4) * mm, "end": v(-1319.1, -3.4) * mm});
            skLineSegment(sketch, "E162.MirrorCS", {"start": v(-1369.1, 223) * mm, "end": v(-1319.1, 223) * mm});
            skLineSegment(sketch, "E163.MirrorCS", {"start": v(-1482.3, 166.4) * mm, "end": v(-1432.3, 166.4) * mm});
            skLineSegment(sketch, "E164.MirrorCS", {"start": v(-1425.7, 81.5) * mm, "end": v(-1375.7, 81.5) * mm});
            skLineSegment(sketch, "E165.MirrorCS", {"start": v(-1538.9, 88.1) * mm, "end": v(-1538.9, 138.1) * mm});
            skLineSegment(sketch, "E166.MirrorCS", {"start": v(-1538.9, 81.5) * mm, "end": v(-1488.9, 81.5) * mm});
            skLineSegment(sketch, "E167.MirrorCS", {"start": v(-1538.9, 31.5) * mm, "end": v(-1488.9, 31.5) * mm});
            skLineSegment(sketch, "E168.MirrorCS", {"start": v(-1488.9, 31.5) * mm, "end": v(-1488.9, 81.5) * mm});
            skLineSegment(sketch, "E169.MirrorCS", {"start": v(-1538.9, 31.5) * mm, "end": v(-1538.9, 81.5) * mm});
            skLineSegment(sketch, "E170.MirrorCS", {"start": v(-1538.9, 24.9) * mm, "end": v(-1488.9, 24.9) * mm});
            skLineSegment(sketch, "E171.MirrorCS", {"start": v(-1538.9, -25.1) * mm, "end": v(-1488.9, -25.1) * mm});
            skLineSegment(sketch, "E172.MirrorCS", {"start": v(-1488.9, -25.1) * mm, "end": v(-1488.9, 24.9) * mm});
            skLineSegment(sketch, "E173.MirrorCS", {"start": v(-1538.9, -25.1) * mm, "end": v(-1538.9, 24.9) * mm});
            skLineSegment(sketch, "E174.MirrorCS", {"start": v(-1488.9, -31.7) * mm, "end": v(-1488.9, -56.7) * mm});
            skLineSegment(sketch, "E175.MirrorCS", {"start": v(-1538.9, -31.7) * mm, "end": v(-1488.9, -31.7) * mm});
            skLineSegment(sketch, "E176.MirrorCS", {"start": v(-1538.9, -56.7) * mm, "end": v(-1538.9, -31.7) * mm});
            skLineSegment(sketch, "E177.MirrorCS", {"start": v(-1538.9, 138.1) * mm, "end": v(-1488.9, 138.1) * mm});
            skLineSegment(sketch, "E178.MirrorCS", {"start": v(-1538.9, 88.1) * mm, "end": v(-1488.9, 88.1) * mm});
            skLineSegment(sketch, "E179.MirrorCS", {"start": v(-1425.7, -25.1) * mm, "end": v(-1375.7, -25.1) * mm});
            skLineSegment(sketch, "E180.MirrorCS", {"start": v(-1488.9, 88.1) * mm, "end": v(-1488.9, 138.1) * mm});
            skLineSegment(sketch, "E181.MirrorCS", {"start": v(-1482.3, 116.4) * mm, "end": v(-1432.3, 116.4) * mm});
            skLineSegment(sketch, "E182.MirrorCS", {"start": v(-1482.3, 53.2) * mm, "end": v(-1432.3, 53.2) * mm});
            skLineSegment(sketch, "E183.MirrorCS", {"start": v(-1425.7, 31.5) * mm, "end": v(-1375.7, 31.5) * mm});
            skLineSegment(sketch, "E184.MirrorCS", {"start": v(-1375.7, -31.7) * mm, "end": v(-1375.7, -56.7) * mm});
            skLineSegment(sketch, "E185.MirrorCS", {"start": v(-1425.7, 194.7) * mm, "end": v(-1375.7, 194.7) * mm});
            skLineSegment(sketch, "E186.MirrorCS", {"start": v(-1369.1, -53.4) * mm, "end": v(-1319.1, -53.4) * mm});
            skLineSegment(sketch, "E187.MirrorCS", {"start": v(-1369.1, 173) * mm, "end": v(-1319.1, 173) * mm});
            skLineSegment(sketch, "E188.MirrorCS", {"start": v(-1369.1, 109.8) * mm, "end": v(-1319.1, 109.8) * mm});
            skLineSegment(sketch, "E189.MirrorCS", {"start": v(-1538.9, 201.3) * mm, "end": v(-1488.9, 201.3) * mm});
            skLineSegment(sketch, "E190.MirrorCS", {"start": v(-1482.3, 116.4) * mm, "end": v(-1482.3, 166.4) * mm});
            skLineSegment(sketch, "E191.MirrorCS", {"start": v(-1432.3, 3.2) * mm, "end": v(-1432.3, 53.2) * mm});
            skLineSegment(sketch, "E192.MirrorCS", {"start": v(-1425.7, 31.5) * mm, "end": v(-1425.7, 81.5) * mm});
            skLineSegment(sketch, "E193.MirrorCS", {"start": v(-1425.7, 88.1) * mm, "end": v(-1375.7, 88.1) * mm});
            skLineSegment(sketch, "E194.MirrorCS", {"start": v(-1482.3, 173) * mm, "end": v(-1432.3, 173) * mm});
            skLineSegment(sketch, "E195.MirrorCS", {"start": v(-1482.3, 223) * mm, "end": v(-1432.3, 223) * mm});
            skLineSegment(sketch, "E196.MirrorCS", {"start": v(-1425.7, 138.1) * mm, "end": v(-1375.7, 138.1) * mm});
            skLineSegment(sketch, "E197.MirrorCS", {"start": v(-1538.9, 201.3) * mm, "end": v(-1538.9, 226.3) * mm});
            skLineSegment(sketch, "E198.MirrorCS", {"start": v(-1482.3, -53.4) * mm, "end": v(-1432.3, -53.4) * mm});
            skLineSegment(sketch, "E199.MirrorCS", {"start": v(-1432.3, 116.4) * mm, "end": v(-1432.3, 166.4) * mm});
            skLineSegment(sketch, "E200.MirrorCS", {"start": v(-1482.3, 3.2) * mm, "end": v(-1432.3, 3.2) * mm});
            skLineSegment(sketch, "E201.MirrorCS", {"start": v(-1482.3, -3.4) * mm, "end": v(-1432.3, -3.4) * mm});
            skLineSegment(sketch, "E202.MirrorCS", {"start": v(-1369.1, 53.2) * mm, "end": v(-1319.1, 53.2) * mm});
            skLineSegment(sketch, "E203.MirrorCS", {"start": v(-1369.1, 173) * mm, "end": v(-1369.1, 223) * mm});
            skLineSegment(sketch, "E204.MirrorCS", {"start": v(-1319.1, 59.8) * mm, "end": v(-1319.1, 109.8) * mm});
            skLineSegment(sketch, "E205.MirrorCS", {"start": v(-1538.9, 194.7) * mm, "end": v(-1488.9, 194.7) * mm});
            skLineSegment(sketch, "E206.MirrorCS", {"start": v(-1369.1, 166.4) * mm, "end": v(-1319.1, 166.4) * mm});
            skLineSegment(sketch, "E207.MirrorCS", {"start": v(-1482.3, 3.2) * mm, "end": v(-1482.3, 53.2) * mm});
            skLineSegment(sketch, "E208.MirrorCS", {"start": v(-1425.7, 144.7) * mm, "end": v(-1425.7, 194.7) * mm});
            skLineSegment(sketch, "E209.MirrorCS", {"start": v(-1369.1, 59.8) * mm, "end": v(-1369.1, 109.8) * mm});
            skLineSegment(sketch, "E210.MirrorCS", {"start": v(-1425.7, -56.7) * mm, "end": v(-1425.7, -31.7) * mm});
            skLineSegment(sketch, "E211.MirrorCS", {"start": v(-1425.7, -31.7) * mm, "end": v(-1375.7, -31.7) * mm});
            skLineSegment(sketch, "E212.MirrorCS", {"start": v(-1375.7, 144.7) * mm, "end": v(-1375.7, 194.7) * mm});
            skLineSegment(sketch, "E213.MirrorCS", {"start": v(-1375.7, 31.5) * mm, "end": v(-1375.7, 81.5) * mm});
            skLineSegment(sketch, "E214.MirrorCS", {"start": v(-1319.1, -53.4) * mm, "end": v(-1319.1, -3.4) * mm});
            skLineSegment(sketch, "E215.MirrorCS", {"start": v(-1482.3, 109.8) * mm, "end": v(-1432.3, 109.8) * mm});
            skLineSegment(sketch, "E216.MirrorCS", {"start": v(-1425.7, 24.9) * mm, "end": v(-1375.7, 24.9) * mm});
            skLineSegment(sketch, "E217.MirrorCS", {"start": v(-1488.9, 201.3) * mm, "end": v(-1488.9, 226.3) * mm});
            skLineSegment(sketch, "E218.MirrorCS", {"start": v(-1369.1, 3.2) * mm, "end": v(-1319.1, 3.2) * mm});
            skLineSegment(sketch, "E219.MirrorCS", {"start": v(-1369.1, 59.8) * mm, "end": v(-1319.1, 59.8) * mm});
            skLineSegment(sketch, "E220.MirrorCS", {"start": v(-1319.1, 173) * mm, "end": v(-1319.1, 223) * mm});
            skLineSegment(sketch, "E221.MirrorCS", {"start": v(-1369.1, -53.4) * mm, "end": v(-1369.1, -3.4) * mm});
            skLineSegment(sketch, "E222.MirrorCS", {"start": v(-1425.7, 144.7) * mm, "end": v(-1375.7, 144.7) * mm});
            skLineSegment(sketch, "E223", {"start": v(-1538.9, 226.3) * mm, "end": v(-1488.9, 226.18) * mm});
            skLineSegment(sketch, "E224.trimOffspring", {"start": v(-1425.7, 226.04) * mm, "end": v(-1375.7, 225.93) * mm});
            skLineSegment(sketch, "E225", {"start": v(-1212.69, -60) * mm, "end": v(-1212.69, -85) * mm});
            skLineSegment(sketch, "E226", {"start": v(-1212.69, -85) * mm, "end": v(-1162.69, -85) * mm});
            skLineSegment(sketch, "E227", {"start": v(-1162.69, -85) * mm, "end": v(-1162.69, -60) * mm});
            skLineSegment(sketch, "E228.bottom", {"start": v(-1212.69, -91.6) * mm, "end": v(-1212.69, -141.6) * mm});
            skLineSegment(sketch, "E228.top", {"start": v(-1162.69, -91.6) * mm, "end": v(-1162.69, -141.6) * mm});
            skLineSegment(sketch, "E228.left", {"start": v(-1212.69, -91.6) * mm, "end": v(-1162.69, -91.6) * mm});
            skLineSegment(sketch, "E228.right", {"start": v(-1212.69, -141.6) * mm, "end": v(-1162.69, -141.6) * mm});
            skLineSegment(sketch, "E229.bottom", {"start": v(-1212.69, -148.2) * mm, "end": v(-1212.69, -198.2) * mm});
            skLineSegment(sketch, "E229.top", {"start": v(-1162.69, -148.2) * mm, "end": v(-1162.69, -198.2) * mm});
            skLineSegment(sketch, "E229.left", {"start": v(-1212.69, -148.2) * mm, "end": v(-1162.69, -148.2) * mm});
            skLineSegment(sketch, "E229.right", {"start": v(-1212.69, -198.2) * mm, "end": v(-1162.69, -198.2) * mm});
            skLineSegment(sketch, "E230.bottom", {"start": v(-1212.69, -204.8) * mm, "end": v(-1212.69, -254.8) * mm});
            skLineSegment(sketch, "E230.top", {"start": v(-1162.69, -204.8) * mm, "end": v(-1162.69, -254.8) * mm});
            skLineSegment(sketch, "E230.left", {"start": v(-1212.69, -204.8) * mm, "end": v(-1162.69, -204.8) * mm});
            skLineSegment(sketch, "E230.right", {"start": v(-1212.69, -254.8) * mm, "end": v(-1162.69, -254.8) * mm});
            skLineSegment(sketch, "E231.bottom", {"start": v(-1212.69, -261.4) * mm, "end": v(-1212.69, -311.4) * mm});
            skLineSegment(sketch, "E231.top", {"start": v(-1162.69, -261.4) * mm, "end": v(-1162.69, -311.4) * mm});
            skLineSegment(sketch, "E231.left", {"start": v(-1212.69, -261.4) * mm, "end": v(-1162.69, -261.4) * mm});
            skLineSegment(sketch, "E231.right", {"start": v(-1212.69, -311.4) * mm, "end": v(-1162.69, -311.4) * mm});
            skLineSegment(sketch, "E232.bottom", {"start": v(-1212.69, -318) * mm, "end": v(-1212.69, -343) * mm});
            skLineSegment(sketch, "E232.top", {"start": v(-1162.69, -318) * mm, "end": v(-1162.69, -343) * mm});
            skLineSegment(sketch, "E232.left", {"start": v(-1212.69, -318) * mm, "end": v(-1162.69, -318) * mm});
            skLineSegment(sketch, "E232.right", {"start": v(-1212.69, -343) * mm, "end": v(-1162.69, -343) * mm});
            skLineSegment(sketch, "E233.bottom", {"start": v(-1156.09, -63.3) * mm, "end": v(-1156.09, -113.3) * mm});
            skLineSegment(sketch, "E233.top", {"start": v(-1106.09, -63.3) * mm, "end": v(-1106.09, -113.3) * mm});
            skLineSegment(sketch, "E233.left", {"start": v(-1156.09, -63.3) * mm, "end": v(-1106.09, -63.3) * mm});
            skLineSegment(sketch, "E233.right", {"start": v(-1156.09, -113.3) * mm, "end": v(-1106.09, -113.3) * mm});
            skLineSegment(sketch, "E234.bottom", {"start": v(-1156.09, -119.9) * mm, "end": v(-1156.09, -169.9) * mm});
            skLineSegment(sketch, "E234.top", {"start": v(-1106.09, -119.9) * mm, "end": v(-1106.09, -169.9) * mm});
            skLineSegment(sketch, "E234.left", {"start": v(-1156.09, -119.9) * mm, "end": v(-1106.09, -119.9) * mm});
            skLineSegment(sketch, "E234.right", {"start": v(-1156.09, -169.9) * mm, "end": v(-1106.09, -169.9) * mm});
            skLineSegment(sketch, "E235.bottom", {"start": v(-1156.09, -176.5) * mm, "end": v(-1156.09, -226.5) * mm});
            skLineSegment(sketch, "E235.top", {"start": v(-1106.09, -176.5) * mm, "end": v(-1106.09, -226.5) * mm});
            skLineSegment(sketch, "E235.left", {"start": v(-1156.09, -176.5) * mm, "end": v(-1106.09, -176.5) * mm});
            skLineSegment(sketch, "E235.right", {"start": v(-1156.09, -226.5) * mm, "end": v(-1106.09, -226.5) * mm});
            skLineSegment(sketch, "E236.bottom", {"start": v(-1156.09, -233.1) * mm, "end": v(-1156.09, -283.1) * mm});
            skLineSegment(sketch, "E236.top", {"start": v(-1106.09, -233.1) * mm, "end": v(-1106.09, -283.1) * mm});
            skLineSegment(sketch, "E236.left", {"start": v(-1156.09, -233.1) * mm, "end": v(-1106.09, -233.1) * mm});
            skLineSegment(sketch, "E236.right", {"start": v(-1156.09, -283.1) * mm, "end": v(-1106.09, -283.1) * mm});
            skLineSegment(sketch, "E237.bottom", {"start": v(-1156.09, -289.7) * mm, "end": v(-1156.09, -339.7) * mm});
            skLineSegment(sketch, "E237.top", {"start": v(-1106.09, -289.7) * mm, "end": v(-1106.09, -339.7) * mm});
            skLineSegment(sketch, "E237.left", {"start": v(-1156.09, -289.7) * mm, "end": v(-1106.09, -289.7) * mm});
            skLineSegment(sketch, "E237.right", {"start": v(-1156.09, -339.7) * mm, "end": v(-1106.09, -339.7) * mm});
            skLineSegment(sketch, "E238", {"start": v(-1099.49, -60) * mm, "end": v(-1099.49, -85) * mm});
            skLineSegment(sketch, "E239", {"start": v(-1099.49, -85) * mm, "end": v(-1049.49, -85) * mm});
            skLineSegment(sketch, "E240", {"start": v(-1049.49, -85) * mm, "end": v(-1049.49, -60) * mm});
            skLineSegment(sketch, "E241.bottom", {"start": v(-1099.49, -91.6) * mm, "end": v(-1099.49, -141.6) * mm});
            skLineSegment(sketch, "E241.top", {"start": v(-1049.49, -91.6) * mm, "end": v(-1049.49, -141.6) * mm});
            skLineSegment(sketch, "E241.left", {"start": v(-1099.49, -91.6) * mm, "end": v(-1049.49, -91.6) * mm});
            skLineSegment(sketch, "E241.right", {"start": v(-1099.49, -141.6) * mm, "end": v(-1049.49, -141.6) * mm});
            skLineSegment(sketch, "E242.bottom", {"start": v(-1099.49, -148.2) * mm, "end": v(-1099.49, -198.2) * mm});
            skLineSegment(sketch, "E242.top", {"start": v(-1049.49, -148.2) * mm, "end": v(-1049.49, -198.2) * mm});
            skLineSegment(sketch, "E242.left", {"start": v(-1099.49, -148.2) * mm, "end": v(-1049.49, -148.2) * mm});
            skLineSegment(sketch, "E242.right", {"start": v(-1099.49, -198.2) * mm, "end": v(-1049.49, -198.2) * mm});
            skLineSegment(sketch, "E243.bottom", {"start": v(-1099.49, -204.8) * mm, "end": v(-1099.49, -254.8) * mm});
            skLineSegment(sketch, "E243.top", {"start": v(-1049.49, -204.8) * mm, "end": v(-1049.49, -254.8) * mm});
            skLineSegment(sketch, "E243.left", {"start": v(-1099.49, -204.8) * mm, "end": v(-1049.49, -204.8) * mm});
            skLineSegment(sketch, "E243.right", {"start": v(-1099.49, -254.8) * mm, "end": v(-1049.49, -254.8) * mm});
            skLineSegment(sketch, "E244.bottom", {"start": v(-1099.49, -261.4) * mm, "end": v(-1099.49, -311.4) * mm});
            skLineSegment(sketch, "E244.top", {"start": v(-1049.49, -261.4) * mm, "end": v(-1049.49, -311.4) * mm});
            skLineSegment(sketch, "E244.left", {"start": v(-1099.49, -261.4) * mm, "end": v(-1049.49, -261.4) * mm});
            skLineSegment(sketch, "E244.right", {"start": v(-1099.49, -311.4) * mm, "end": v(-1049.49, -311.4) * mm});
            skLineSegment(sketch, "E245.bottom", {"start": v(-1099.49, -318) * mm, "end": v(-1099.49, -343) * mm});
            skLineSegment(sketch, "E245.top", {"start": v(-1049.49, -318) * mm, "end": v(-1049.49, -343) * mm});
            skLineSegment(sketch, "E245.left", {"start": v(-1099.49, -318) * mm, "end": v(-1049.49, -318) * mm});
            skLineSegment(sketch, "E245.right", {"start": v(-1099.49, -343) * mm, "end": v(-1049.49, -343) * mm});
            skLineSegment(sketch, "E246.bottom", {"start": v(-1042.89, -63.3) * mm, "end": v(-1042.89, -113.3) * mm});
            skLineSegment(sketch, "E246.top", {"start": v(-992.89, -63.3) * mm, "end": v(-992.89, -113.3) * mm});
            skLineSegment(sketch, "E246.left", {"start": v(-1042.89, -63.3) * mm, "end": v(-992.89, -63.3) * mm});
            skLineSegment(sketch, "E246.right", {"start": v(-1042.89, -113.3) * mm, "end": v(-992.89, -113.3) * mm});
            skLineSegment(sketch, "E247.bottom", {"start": v(-1042.89, -119.9) * mm, "end": v(-1042.89, -169.9) * mm});
            skLineSegment(sketch, "E247.top", {"start": v(-992.89, -119.9) * mm, "end": v(-992.89, -169.9) * mm});
            skLineSegment(sketch, "E247.left", {"start": v(-1042.89, -119.9) * mm, "end": v(-992.89, -119.9) * mm});
            skLineSegment(sketch, "E247.right", {"start": v(-1042.89, -169.9) * mm, "end": v(-992.89, -169.9) * mm});
            skLineSegment(sketch, "E248.bottom", {"start": v(-1042.89, -176.5) * mm, "end": v(-1042.89, -226.5) * mm});
            skLineSegment(sketch, "E248.top", {"start": v(-992.89, -176.5) * mm, "end": v(-992.89, -226.5) * mm});
            skLineSegment(sketch, "E248.left", {"start": v(-1042.89, -176.5) * mm, "end": v(-992.89, -176.5) * mm});
            skLineSegment(sketch, "E248.right", {"start": v(-1042.89, -226.5) * mm, "end": v(-992.89, -226.5) * mm});
            skLineSegment(sketch, "E249.bottom", {"start": v(-1042.89, -233.1) * mm, "end": v(-1042.89, -283.1) * mm});
            skLineSegment(sketch, "E249.top", {"start": v(-992.89, -233.1) * mm, "end": v(-992.89, -283.1) * mm});
            skLineSegment(sketch, "E249.left", {"start": v(-1042.89, -233.1) * mm, "end": v(-992.89, -233.1) * mm});
            skLineSegment(sketch, "E249.right", {"start": v(-1042.89, -283.1) * mm, "end": v(-992.89, -283.1) * mm});
            skLineSegment(sketch, "E250.bottom", {"start": v(-1042.89, -289.7) * mm, "end": v(-1042.89, -339.7) * mm});
            skLineSegment(sketch, "E250.top", {"start": v(-992.89, -289.7) * mm, "end": v(-992.89, -339.7) * mm});
            skLineSegment(sketch, "E250.left", {"start": v(-1042.89, -289.7) * mm, "end": v(-992.89, -289.7) * mm});
            skLineSegment(sketch, "E250.right", {"start": v(-1042.89, -339.7) * mm, "end": v(-992.89, -339.7) * mm});
            skLineSegment(sketch, "E251.MirrorCS", {"start": v(-1099.49, 198) * mm, "end": v(-1049.49, 198) * mm});
            skLineSegment(sketch, "E252.MirrorCS", {"start": v(-1042.89, 113.1) * mm, "end": v(-992.89, 113.1) * mm});
            skLineSegment(sketch, "E253.MirrorCS", {"start": v(-1212.69, 141.4) * mm, "end": v(-1162.69, 141.4) * mm});
            skLineSegment(sketch, "E254.MirrorCS", {"start": v(-992.89, -0.1) * mm, "end": v(-992.89, 49.9) * mm});
            skLineSegment(sketch, "E255.MirrorCS", {"start": v(-1106.09, -56.7) * mm, "end": v(-1106.09, -6.7) * mm});
            skLineSegment(sketch, "E256.MirrorCS", {"start": v(-1106.09, 169.7) * mm, "end": v(-1106.09, 219.7) * mm});
            skLineSegment(sketch, "E257.MirrorCS", {"start": v(-1049.49, 84.8) * mm, "end": v(-1049.49, 134.8) * mm});
            skLineSegment(sketch, "E258.MirrorCS", {"start": v(-1106.09, 56.5) * mm, "end": v(-1106.09, 106.5) * mm});
            skLineSegment(sketch, "E259.MirrorCS", {"start": v(-1049.49, -28.4) * mm, "end": v(-1049.49, 21.6) * mm});
            skLineSegment(sketch, "E260.MirrorCS", {"start": v(-1049.49, 198) * mm, "end": v(-1049.49, 223) * mm});
            skLineSegment(sketch, "E261.MirrorCS", {"start": v(-992.89, 113.1) * mm, "end": v(-992.89, 163.1) * mm});
            skLineSegment(sketch, "E262.MirrorCS", {"start": v(-1162.69, 141.4) * mm, "end": v(-1162.69, 191.4) * mm});
            skLineSegment(sketch, "E263.MirrorCS", {"start": v(-1042.89, -0.1) * mm, "end": v(-1042.89, 49.9) * mm});
            skLineSegment(sketch, "E264.MirrorCS", {"start": v(-1156.09, 56.5) * mm, "end": v(-1106.09, 56.5) * mm});
            skLineSegment(sketch, "E265.MirrorCS", {"start": v(-1156.09, -56.7) * mm, "end": v(-1156.09, -6.7) * mm});
            skLineSegment(sketch, "E266.MirrorCS", {"start": v(-1156.09, 169.7) * mm, "end": v(-1156.09, 219.7) * mm});
            skLineSegment(sketch, "E267.MirrorCS", {"start": v(-1099.49, 84.8) * mm, "end": v(-1099.49, 134.8) * mm});
            skLineSegment(sketch, "E268.MirrorCS", {"start": v(-1156.09, 56.5) * mm, "end": v(-1156.09, 106.5) * mm});
            skLineSegment(sketch, "E269.MirrorCS", {"start": v(-1099.49, -28.4) * mm, "end": v(-1099.49, 21.6) * mm});
            skLineSegment(sketch, "E270.MirrorCS", {"start": v(-1099.49, 198) * mm, "end": v(-1099.49, 223) * mm});
            skLineSegment(sketch, "E271.MirrorCS", {"start": v(-1042.89, 113.1) * mm, "end": v(-1042.89, 163.1) * mm});
            skLineSegment(sketch, "E272.MirrorCS", {"start": v(-1212.69, 141.4) * mm, "end": v(-1212.69, 191.4) * mm});
            skLineSegment(sketch, "E273.MirrorCS", {"start": v(-1042.89, -6.7) * mm, "end": v(-992.89, -6.7) * mm});
            skLineSegment(sketch, "E274.MirrorCS", {"start": v(-1042.89, 219.7) * mm, "end": v(-992.89, 219.7) * mm});
            skLineSegment(sketch, "E275.MirrorCS", {"start": v(-1156.09, 163.1) * mm, "end": v(-1106.09, 163.1) * mm});
            skLineSegment(sketch, "E276.MirrorCS", {"start": v(-1099.49, 78.2) * mm, "end": v(-1049.49, 78.2) * mm});
            skLineSegment(sketch, "E277.MirrorCS", {"start": v(-1212.69, 84.8) * mm, "end": v(-1212.69, 134.8) * mm});
            skLineSegment(sketch, "E278.MirrorCS", {"start": v(-1212.69, 78.2) * mm, "end": v(-1162.69, 78.2) * mm});
            skLineSegment(sketch, "E279.MirrorCS", {"start": v(-1212.69, 28.2) * mm, "end": v(-1162.69, 28.2) * mm});
            skLineSegment(sketch, "E280.MirrorCS", {"start": v(-1162.69, 28.2) * mm, "end": v(-1162.69, 78.2) * mm});
            skLineSegment(sketch, "E281.MirrorCS", {"start": v(-1212.69, 28.2) * mm, "end": v(-1212.69, 78.2) * mm});
            skLineSegment(sketch, "E282.MirrorCS", {"start": v(-1212.69, 21.6) * mm, "end": v(-1162.69, 21.6) * mm});
            skLineSegment(sketch, "E283.MirrorCS", {"start": v(-1212.69, -28.4) * mm, "end": v(-1162.69, -28.4) * mm});
            skLineSegment(sketch, "E284.MirrorCS", {"start": v(-1162.69, -28.4) * mm, "end": v(-1162.69, 21.6) * mm});
            skLineSegment(sketch, "E285.MirrorCS", {"start": v(-1212.69, -28.4) * mm, "end": v(-1212.69, 21.6) * mm});
            skLineSegment(sketch, "E286.MirrorCS", {"start": v(-1162.69, -35) * mm, "end": v(-1162.69, -60) * mm});
            skLineSegment(sketch, "E287.MirrorCS", {"start": v(-1212.69, -35) * mm, "end": v(-1162.69, -35) * mm});
            skLineSegment(sketch, "E288.MirrorCS", {"start": v(-1212.69, -60) * mm, "end": v(-1212.69, -35) * mm});
            skLineSegment(sketch, "E289.MirrorCS", {"start": v(-1212.69, 134.8) * mm, "end": v(-1162.69, 134.8) * mm});
            skLineSegment(sketch, "E290.MirrorCS", {"start": v(-1212.69, 84.8) * mm, "end": v(-1162.69, 84.8) * mm});
            skLineSegment(sketch, "E291.MirrorCS", {"start": v(-1099.49, -28.4) * mm, "end": v(-1049.49, -28.4) * mm});
            skLineSegment(sketch, "E292.MirrorCS", {"start": v(-1162.69, 84.8) * mm, "end": v(-1162.69, 134.8) * mm});
            skLineSegment(sketch, "E293.MirrorCS", {"start": v(-1156.09, 113.1) * mm, "end": v(-1106.09, 113.1) * mm});
            skLineSegment(sketch, "E294.MirrorCS", {"start": v(-1156.09, 49.9) * mm, "end": v(-1106.09, 49.9) * mm});
            skLineSegment(sketch, "E295.MirrorCS", {"start": v(-1099.49, 28.2) * mm, "end": v(-1049.49, 28.2) * mm});
            skLineSegment(sketch, "E296.MirrorCS", {"start": v(-1049.49, -35) * mm, "end": v(-1049.49, -60) * mm});
            skLineSegment(sketch, "E297.MirrorCS", {"start": v(-1099.49, 191.4) * mm, "end": v(-1049.49, 191.4) * mm});
            skLineSegment(sketch, "E298.MirrorCS", {"start": v(-1042.89, -56.7) * mm, "end": v(-992.89, -56.7) * mm});
            skLineSegment(sketch, "E299.MirrorCS", {"start": v(-1042.89, 169.7) * mm, "end": v(-992.89, 169.7) * mm});
            skLineSegment(sketch, "E300.MirrorCS", {"start": v(-1042.89, 106.5) * mm, "end": v(-992.89, 106.5) * mm});
            skLineSegment(sketch, "E301.MirrorCS", {"start": v(-1212.69, 198) * mm, "end": v(-1162.69, 198) * mm});
            skLineSegment(sketch, "E302.MirrorCS", {"start": v(-1156.09, 113.1) * mm, "end": v(-1156.09, 163.1) * mm});
            skLineSegment(sketch, "E303.MirrorCS", {"start": v(-1106.09, -0.1) * mm, "end": v(-1106.09, 49.9) * mm});
            skLineSegment(sketch, "E304.MirrorCS", {"start": v(-1099.49, 28.2) * mm, "end": v(-1099.49, 78.2) * mm});
            skLineSegment(sketch, "E305.MirrorCS", {"start": v(-1099.49, 84.8) * mm, "end": v(-1049.49, 84.8) * mm});
            skLineSegment(sketch, "E306.MirrorCS", {"start": v(-1156.09, 169.7) * mm, "end": v(-1106.09, 169.7) * mm});
            skLineSegment(sketch, "E307.MirrorCS", {"start": v(-1156.09, 219.7) * mm, "end": v(-1106.09, 219.7) * mm});
            skLineSegment(sketch, "E308.MirrorCS", {"start": v(-1099.49, 134.8) * mm, "end": v(-1049.49, 134.8) * mm});
            skLineSegment(sketch, "E309.MirrorCS", {"start": v(-1212.69, 198) * mm, "end": v(-1212.69, 223) * mm});
            skLineSegment(sketch, "E310.MirrorCS", {"start": v(-1156.09, -56.7) * mm, "end": v(-1106.09, -56.7) * mm});
            skLineSegment(sketch, "E311.MirrorCS", {"start": v(-1106.09, 113.1) * mm, "end": v(-1106.09, 163.1) * mm});
            skLineSegment(sketch, "E312.MirrorCS", {"start": v(-1156.09, -0.1) * mm, "end": v(-1106.09, -0.1) * mm});
            skLineSegment(sketch, "E313.MirrorCS", {"start": v(-1156.09, -6.7) * mm, "end": v(-1106.09, -6.7) * mm});
            skLineSegment(sketch, "E314.MirrorCS", {"start": v(-1042.89, 49.9) * mm, "end": v(-992.89, 49.9) * mm});
            skLineSegment(sketch, "E315.MirrorCS", {"start": v(-1042.89, 169.7) * mm, "end": v(-1042.89, 219.7) * mm});
            skLineSegment(sketch, "E316.MirrorCS", {"start": v(-992.89, 56.5) * mm, "end": v(-992.89, 106.5) * mm});
            skLineSegment(sketch, "E317.MirrorCS", {"start": v(-1212.69, 191.4) * mm, "end": v(-1162.69, 191.4) * mm});
            skLineSegment(sketch, "E318.MirrorCS", {"start": v(-1042.89, 163.1) * mm, "end": v(-992.89, 163.1) * mm});
            skLineSegment(sketch, "E319.MirrorCS", {"start": v(-1156.09, -0.1) * mm, "end": v(-1156.09, 49.9) * mm});
            skLineSegment(sketch, "E320.MirrorCS", {"start": v(-1099.49, 223) * mm, "end": v(-1049.49, 223) * mm});
            skLineSegment(sketch, "E321.MirrorCS", {"start": v(-1099.49, 141.4) * mm, "end": v(-1099.49, 191.4) * mm});
            skLineSegment(sketch, "E322.MirrorCS", {"start": v(-1042.89, 56.5) * mm, "end": v(-1042.89, 106.5) * mm});
            skLineSegment(sketch, "E323.MirrorCS", {"start": v(-1099.49, -60) * mm, "end": v(-1099.49, -35) * mm});
            skLineSegment(sketch, "E324.MirrorCS", {"start": v(-1099.49, -35) * mm, "end": v(-1049.49, -35) * mm});
            skLineSegment(sketch, "E325.MirrorCS", {"start": v(-1049.49, 141.4) * mm, "end": v(-1049.49, 191.4) * mm});
            skLineSegment(sketch, "E326.MirrorCS", {"start": v(-1049.49, 28.2) * mm, "end": v(-1049.49, 78.2) * mm});
            skLineSegment(sketch, "E327.MirrorCS", {"start": v(-992.89, -56.7) * mm, "end": v(-992.89, -6.7) * mm});
            skLineSegment(sketch, "E328.MirrorCS", {"start": v(-1156.09, 106.5) * mm, "end": v(-1106.09, 106.5) * mm});
            skLineSegment(sketch, "E329.MirrorCS", {"start": v(-1099.49, 21.6) * mm, "end": v(-1049.49, 21.6) * mm});
            skLineSegment(sketch, "E330.MirrorCS", {"start": v(-1162.69, 198) * mm, "end": v(-1162.69, 223) * mm});
            skLineSegment(sketch, "E331.MirrorCS", {"start": v(-1042.89, -0.1) * mm, "end": v(-992.89, -0.1) * mm});
            skLineSegment(sketch, "E332.MirrorCS", {"start": v(-1042.89, 56.5) * mm, "end": v(-992.89, 56.5) * mm});
            skLineSegment(sketch, "E333.MirrorCS", {"start": v(-992.89, 169.7) * mm, "end": v(-992.89, 219.7) * mm});
            skLineSegment(sketch, "E334.MirrorCS", {"start": v(-1042.89, -56.7) * mm, "end": v(-1042.89, -6.7) * mm});
            skLineSegment(sketch, "E335.MirrorCS", {"start": v(-1099.49, 141.4) * mm, "end": v(-1049.49, 141.4) * mm});
            skPoint(sketch, "E336.end.orphan", {"position": v(-1039.52, -60) * mm});
            skLineSegment(sketch, "E337", {"start": v(-1212.69, 223) * mm, "end": v(-1162.69, 222.88) * mm});
            skLineSegment(sketch, "E338", {"start": v(-929.6, -63.3) * mm, "end": v(-929.6, -88.3) * mm});
            skLineSegment(sketch, "E339", {"start": v(-929.6, -88.3) * mm, "end": v(-879.6, -88.3) * mm});
            skLineSegment(sketch, "E340", {"start": v(-879.6, -88.3) * mm, "end": v(-879.6, -63.3) * mm});
            skLineSegment(sketch, "E341.bottom", {"start": v(-929.6, -94.9) * mm, "end": v(-929.6, -144.9) * mm});
            skLineSegment(sketch, "E341.top", {"start": v(-879.6, -94.9) * mm, "end": v(-879.6, -144.9) * mm});
            skLineSegment(sketch, "E341.left", {"start": v(-929.6, -94.9) * mm, "end": v(-879.6, -94.9) * mm});
            skLineSegment(sketch, "E341.right", {"start": v(-929.6, -144.9) * mm, "end": v(-879.6, -144.9) * mm});
            skLineSegment(sketch, "E342.bottom", {"start": v(-929.6, -151.5) * mm, "end": v(-929.6, -201.5) * mm});
            skLineSegment(sketch, "E342.top", {"start": v(-879.6, -151.5) * mm, "end": v(-879.6, -201.5) * mm});
            skLineSegment(sketch, "E342.left", {"start": v(-929.6, -151.5) * mm, "end": v(-879.6, -151.5) * mm});
            skLineSegment(sketch, "E342.right", {"start": v(-929.6, -201.5) * mm, "end": v(-879.6, -201.5) * mm});
            skLineSegment(sketch, "E343.bottom", {"start": v(-929.6, -208.1) * mm, "end": v(-929.6, -258.1) * mm});
            skLineSegment(sketch, "E343.top", {"start": v(-879.6, -208.1) * mm, "end": v(-879.6, -258.1) * mm});
            skLineSegment(sketch, "E343.left", {"start": v(-929.6, -208.1) * mm, "end": v(-879.6, -208.1) * mm});
            skLineSegment(sketch, "E343.right", {"start": v(-929.6, -258.1) * mm, "end": v(-879.6, -258.1) * mm});
            skLineSegment(sketch, "E344.bottom", {"start": v(-929.6, -264.7) * mm, "end": v(-929.6, -314.7) * mm});
            skLineSegment(sketch, "E344.top", {"start": v(-879.6, -264.7) * mm, "end": v(-879.6, -314.7) * mm});
            skLineSegment(sketch, "E344.left", {"start": v(-929.6, -264.7) * mm, "end": v(-879.6, -264.7) * mm});
            skLineSegment(sketch, "E344.right", {"start": v(-929.6, -314.7) * mm, "end": v(-879.6, -314.7) * mm});
            skLineSegment(sketch, "E345.bottom", {"start": v(-929.6, -321.3) * mm, "end": v(-929.6, -346.3) * mm});
            skLineSegment(sketch, "E345.top", {"start": v(-879.6, -321.3) * mm, "end": v(-879.6, -346.3) * mm});
            skLineSegment(sketch, "E345.left", {"start": v(-929.6, -321.3) * mm, "end": v(-879.6, -321.3) * mm});
            skLineSegment(sketch, "E345.right", {"start": v(-929.6, -346.3) * mm, "end": v(-879.6, -346.3) * mm});
            skLineSegment(sketch, "E346.bottom", {"start": v(-873, -66.6) * mm, "end": v(-873, -116.6) * mm});
            skLineSegment(sketch, "E346.top", {"start": v(-823, -66.6) * mm, "end": v(-823, -116.6) * mm});
            skLineSegment(sketch, "E346.left", {"start": v(-873, -66.6) * mm, "end": v(-823, -66.6) * mm});
            skLineSegment(sketch, "E346.right", {"start": v(-873, -116.6) * mm, "end": v(-823, -116.6) * mm});
            skLineSegment(sketch, "E347.bottom", {"start": v(-873, -123.2) * mm, "end": v(-873, -173.2) * mm});
            skLineSegment(sketch, "E347.top", {"start": v(-823, -123.2) * mm, "end": v(-823, -173.2) * mm});
            skLineSegment(sketch, "E347.left", {"start": v(-873, -123.2) * mm, "end": v(-823, -123.2) * mm});
            skLineSegment(sketch, "E347.right", {"start": v(-873, -173.2) * mm, "end": v(-823, -173.2) * mm});
            skLineSegment(sketch, "E348.bottom", {"start": v(-873, -179.8) * mm, "end": v(-873, -229.8) * mm});
            skLineSegment(sketch, "E348.top", {"start": v(-823, -179.8) * mm, "end": v(-823, -229.8) * mm});
            skLineSegment(sketch, "E348.left", {"start": v(-873, -179.8) * mm, "end": v(-823, -179.8) * mm});
            skLineSegment(sketch, "E348.right", {"start": v(-873, -229.8) * mm, "end": v(-823, -229.8) * mm});
            skLineSegment(sketch, "E349.bottom", {"start": v(-873, -236.4) * mm, "end": v(-873, -286.4) * mm});
            skLineSegment(sketch, "E349.top", {"start": v(-823, -236.4) * mm, "end": v(-823, -286.4) * mm});
            skLineSegment(sketch, "E349.left", {"start": v(-873, -236.4) * mm, "end": v(-823, -236.4) * mm});
            skLineSegment(sketch, "E349.right", {"start": v(-873, -286.4) * mm, "end": v(-823, -286.4) * mm});
            skLineSegment(sketch, "E350.bottom", {"start": v(-873, -293) * mm, "end": v(-873, -343) * mm});
            skLineSegment(sketch, "E350.top", {"start": v(-823, -293) * mm, "end": v(-823, -343) * mm});
            skLineSegment(sketch, "E350.left", {"start": v(-873, -293) * mm, "end": v(-823, -293) * mm});
            skLineSegment(sketch, "E350.right", {"start": v(-873, -343) * mm, "end": v(-823, -343) * mm});
            skLineSegment(sketch, "E351", {"start": v(-816.4, -63.3) * mm, "end": v(-816.4, -88.3) * mm});
            skLineSegment(sketch, "E352", {"start": v(-816.4, -88.3) * mm, "end": v(-766.4, -88.3) * mm});
            skLineSegment(sketch, "E353", {"start": v(-766.4, -88.3) * mm, "end": v(-766.4, -63.3) * mm});
            skLineSegment(sketch, "E354.bottom", {"start": v(-816.4, -94.9) * mm, "end": v(-816.4, -144.9) * mm});
            skLineSegment(sketch, "E354.top", {"start": v(-766.4, -94.9) * mm, "end": v(-766.4, -144.9) * mm});
            skLineSegment(sketch, "E354.left", {"start": v(-816.4, -94.9) * mm, "end": v(-766.4, -94.9) * mm});
            skLineSegment(sketch, "E354.right", {"start": v(-816.4, -144.9) * mm, "end": v(-766.4, -144.9) * mm});
            skLineSegment(sketch, "E355.bottom", {"start": v(-816.4, -151.5) * mm, "end": v(-816.4, -201.5) * mm});
            skLineSegment(sketch, "E355.top", {"start": v(-766.4, -151.5) * mm, "end": v(-766.4, -201.5) * mm});
            skLineSegment(sketch, "E355.left", {"start": v(-816.4, -151.5) * mm, "end": v(-766.4, -151.5) * mm});
            skLineSegment(sketch, "E355.right", {"start": v(-816.4, -201.5) * mm, "end": v(-766.4, -201.5) * mm});
            skLineSegment(sketch, "E356.bottom", {"start": v(-816.4, -208.1) * mm, "end": v(-816.4, -258.1) * mm});
            skLineSegment(sketch, "E356.top", {"start": v(-766.4, -208.1) * mm, "end": v(-766.4, -258.1) * mm});
            skLineSegment(sketch, "E356.left", {"start": v(-816.4, -208.1) * mm, "end": v(-766.4, -208.1) * mm});
            skLineSegment(sketch, "E356.right", {"start": v(-816.4, -258.1) * mm, "end": v(-766.4, -258.1) * mm});
            skLineSegment(sketch, "E357.bottom", {"start": v(-816.4, -264.7) * mm, "end": v(-816.4, -314.7) * mm});
            skLineSegment(sketch, "E357.top", {"start": v(-766.4, -264.7) * mm, "end": v(-766.4, -314.7) * mm});
            skLineSegment(sketch, "E357.left", {"start": v(-816.4, -264.7) * mm, "end": v(-766.4, -264.7) * mm});
            skLineSegment(sketch, "E357.right", {"start": v(-816.4, -314.7) * mm, "end": v(-766.4, -314.7) * mm});
            skLineSegment(sketch, "E358.bottom", {"start": v(-816.4, -321.3) * mm, "end": v(-816.4, -346.3) * mm});
            skLineSegment(sketch, "E358.top", {"start": v(-766.4, -321.3) * mm, "end": v(-766.4, -346.3) * mm});
            skLineSegment(sketch, "E358.left", {"start": v(-816.4, -321.3) * mm, "end": v(-766.4, -321.3) * mm});
            skLineSegment(sketch, "E358.right", {"start": v(-816.4, -346.3) * mm, "end": v(-766.4, -346.3) * mm});
            skLineSegment(sketch, "E359.bottom", {"start": v(-759.8, -66.6) * mm, "end": v(-759.8, -116.6) * mm});
            skLineSegment(sketch, "E359.top", {"start": v(-709.8, -66.6) * mm, "end": v(-709.8, -116.6) * mm});
            skLineSegment(sketch, "E359.left", {"start": v(-759.8, -66.6) * mm, "end": v(-709.8, -66.6) * mm});
            skLineSegment(sketch, "E359.right", {"start": v(-759.8, -116.6) * mm, "end": v(-709.8, -116.6) * mm});
            skLineSegment(sketch, "E360.bottom", {"start": v(-759.8, -123.2) * mm, "end": v(-759.8, -173.2) * mm});
            skLineSegment(sketch, "E360.top", {"start": v(-709.8, -123.2) * mm, "end": v(-709.8, -173.2) * mm});
            skLineSegment(sketch, "E360.left", {"start": v(-759.8, -123.2) * mm, "end": v(-709.8, -123.2) * mm});
            skLineSegment(sketch, "E360.right", {"start": v(-759.8, -173.2) * mm, "end": v(-709.8, -173.2) * mm});
            skLineSegment(sketch, "E361.bottom", {"start": v(-759.8, -179.8) * mm, "end": v(-759.8, -229.8) * mm});
            skLineSegment(sketch, "E361.top", {"start": v(-709.8, -179.8) * mm, "end": v(-709.8, -229.8) * mm});
            skLineSegment(sketch, "E361.left", {"start": v(-759.8, -179.8) * mm, "end": v(-709.8, -179.8) * mm});
            skLineSegment(sketch, "E361.right", {"start": v(-759.8, -229.8) * mm, "end": v(-709.8, -229.8) * mm});
            skLineSegment(sketch, "E362.bottom", {"start": v(-759.8, -236.4) * mm, "end": v(-759.8, -286.4) * mm});
            skLineSegment(sketch, "E362.top", {"start": v(-709.8, -236.4) * mm, "end": v(-709.8, -286.4) * mm});
            skLineSegment(sketch, "E362.left", {"start": v(-759.8, -236.4) * mm, "end": v(-709.8, -236.4) * mm});
            skLineSegment(sketch, "E362.right", {"start": v(-759.8, -286.4) * mm, "end": v(-709.8, -286.4) * mm});
            skLineSegment(sketch, "E363.bottom", {"start": v(-759.8, -293) * mm, "end": v(-759.8, -343) * mm});
            skLineSegment(sketch, "E363.top", {"start": v(-709.8, -293) * mm, "end": v(-709.8, -343) * mm});
            skLineSegment(sketch, "E363.left", {"start": v(-759.8, -293) * mm, "end": v(-709.8, -293) * mm});
            skLineSegment(sketch, "E363.right", {"start": v(-759.8, -343) * mm, "end": v(-709.8, -343) * mm});
            skLineSegment(sketch, "E364.MirrorCS", {"start": v(-816.4, 194.7) * mm, "end": v(-766.4, 194.7) * mm});
            skLineSegment(sketch, "E365.MirrorCS", {"start": v(-759.8, 109.8) * mm, "end": v(-709.8, 109.8) * mm});
            skLineSegment(sketch, "E366.MirrorCS", {"start": v(-929.6, 138.1) * mm, "end": v(-879.6, 138.1) * mm});
            skLineSegment(sketch, "E367.MirrorCS", {"start": v(-709.8, -3.4) * mm, "end": v(-709.8, 46.6) * mm});
            skLineSegment(sketch, "E368.MirrorCS", {"start": v(-823, -60) * mm, "end": v(-823, -10) * mm});
            skLineSegment(sketch, "E369.MirrorCS", {"start": v(-823, 166.4) * mm, "end": v(-823, 216.4) * mm});
            skLineSegment(sketch, "E370.MirrorCS", {"start": v(-766.4, 81.5) * mm, "end": v(-766.4, 131.5) * mm});
            skLineSegment(sketch, "E371.MirrorCS", {"start": v(-823, 53.2) * mm, "end": v(-823, 103.2) * mm});
            skLineSegment(sketch, "E372.MirrorCS", {"start": v(-766.4, -31.7) * mm, "end": v(-766.4, 18.3) * mm});
            skLineSegment(sketch, "E373.MirrorCS", {"start": v(-766.4, 194.7) * mm, "end": v(-766.4, 219.7) * mm});
            skLineSegment(sketch, "E374.MirrorCS", {"start": v(-709.8, 109.8) * mm, "end": v(-709.8, 159.8) * mm});
            skLineSegment(sketch, "E375.MirrorCS", {"start": v(-879.6, 138.1) * mm, "end": v(-879.6, 188.1) * mm});
            skLineSegment(sketch, "E376.MirrorCS", {"start": v(-759.8, -3.4) * mm, "end": v(-759.8, 46.6) * mm});
            skLineSegment(sketch, "E377.MirrorCS", {"start": v(-873, 53.2) * mm, "end": v(-823, 53.2) * mm});
            skLineSegment(sketch, "E378.MirrorCS", {"start": v(-873, -60) * mm, "end": v(-873, -10) * mm});
            skLineSegment(sketch, "E379.MirrorCS", {"start": v(-873, 166.4) * mm, "end": v(-873, 216.4) * mm});
            skLineSegment(sketch, "E380.MirrorCS", {"start": v(-816.4, 81.5) * mm, "end": v(-816.4, 131.5) * mm});
            skLineSegment(sketch, "E381.MirrorCS", {"start": v(-873, 53.2) * mm, "end": v(-873, 103.2) * mm});
            skLineSegment(sketch, "E382.MirrorCS", {"start": v(-816.4, -31.7) * mm, "end": v(-816.4, 18.3) * mm});
            skLineSegment(sketch, "E383.MirrorCS", {"start": v(-816.4, 194.7) * mm, "end": v(-816.4, 219.7) * mm});
            skLineSegment(sketch, "E384.MirrorCS", {"start": v(-759.8, 109.8) * mm, "end": v(-759.8, 159.8) * mm});
            skLineSegment(sketch, "E385.MirrorCS", {"start": v(-929.6, 138.1) * mm, "end": v(-929.6, 188.1) * mm});
            skLineSegment(sketch, "E386.MirrorCS", {"start": v(-759.8, -10) * mm, "end": v(-709.8, -10) * mm});
            skLineSegment(sketch, "E387.MirrorCS", {"start": v(-759.8, 216.4) * mm, "end": v(-709.8, 216.4) * mm});
            skLineSegment(sketch, "E388.MirrorCS", {"start": v(-873, 159.8) * mm, "end": v(-823, 159.8) * mm});
            skLineSegment(sketch, "E389.MirrorCS", {"start": v(-816.4, 74.9) * mm, "end": v(-766.4, 74.9) * mm});
            skLineSegment(sketch, "E390.MirrorCS", {"start": v(-929.6, 81.5) * mm, "end": v(-929.6, 131.5) * mm});
            skLineSegment(sketch, "E391.MirrorCS", {"start": v(-929.6, 74.9) * mm, "end": v(-879.6, 74.9) * mm});
            skLineSegment(sketch, "E392.MirrorCS", {"start": v(-929.6, 24.9) * mm, "end": v(-879.6, 24.9) * mm});
            skLineSegment(sketch, "E393.MirrorCS", {"start": v(-879.6, 24.9) * mm, "end": v(-879.6, 74.9) * mm});
            skLineSegment(sketch, "E394.MirrorCS", {"start": v(-929.6, 24.9) * mm, "end": v(-929.6, 74.9) * mm});
            skLineSegment(sketch, "E395.MirrorCS", {"start": v(-929.6, 18.3) * mm, "end": v(-879.6, 18.3) * mm});
            skLineSegment(sketch, "E396.MirrorCS", {"start": v(-929.6, -31.7) * mm, "end": v(-879.6, -31.7) * mm});
            skLineSegment(sketch, "E397.MirrorCS", {"start": v(-879.6, -31.7) * mm, "end": v(-879.6, 18.3) * mm});
            skLineSegment(sketch, "E398.MirrorCS", {"start": v(-929.6, -31.7) * mm, "end": v(-929.6, 18.3) * mm});
            skLineSegment(sketch, "E399.MirrorCS", {"start": v(-879.6, -38.3) * mm, "end": v(-879.6, -63.3) * mm});
            skLineSegment(sketch, "E400.MirrorCS", {"start": v(-929.6, -38.3) * mm, "end": v(-879.6, -38.3) * mm});
            skLineSegment(sketch, "E401.MirrorCS", {"start": v(-929.6, -63.3) * mm, "end": v(-929.6, -38.3) * mm});
            skLineSegment(sketch, "E402.MirrorCS", {"start": v(-929.6, 131.5) * mm, "end": v(-879.6, 131.5) * mm});
            skLineSegment(sketch, "E403.MirrorCS", {"start": v(-929.6, 81.5) * mm, "end": v(-879.6, 81.5) * mm});
            skLineSegment(sketch, "E404.MirrorCS", {"start": v(-816.4, -31.7) * mm, "end": v(-766.4, -31.7) * mm});
            skLineSegment(sketch, "E405.MirrorCS", {"start": v(-879.6, 81.5) * mm, "end": v(-879.6, 131.5) * mm});
            skLineSegment(sketch, "E406.MirrorCS", {"start": v(-873, 109.8) * mm, "end": v(-823, 109.8) * mm});
            skLineSegment(sketch, "E407.MirrorCS", {"start": v(-873, 46.6) * mm, "end": v(-823, 46.6) * mm});
            skLineSegment(sketch, "E408.MirrorCS", {"start": v(-816.4, 24.9) * mm, "end": v(-766.4, 24.9) * mm});
            skLineSegment(sketch, "E409.MirrorCS", {"start": v(-766.4, -38.3) * mm, "end": v(-766.4, -63.3) * mm});
            skLineSegment(sketch, "E410.MirrorCS", {"start": v(-816.4, 188.1) * mm, "end": v(-766.4, 188.1) * mm});
            skLineSegment(sketch, "E411.MirrorCS", {"start": v(-759.8, -60) * mm, "end": v(-709.8, -60) * mm});
            skLineSegment(sketch, "E412.MirrorCS", {"start": v(-759.8, 166.4) * mm, "end": v(-709.8, 166.4) * mm});
            skLineSegment(sketch, "E413.MirrorCS", {"start": v(-759.8, 103.2) * mm, "end": v(-709.8, 103.2) * mm});
            skLineSegment(sketch, "E414.MirrorCS", {"start": v(-929.6, 194.7) * mm, "end": v(-879.6, 194.7) * mm});
            skLineSegment(sketch, "E415.MirrorCS", {"start": v(-873, 109.8) * mm, "end": v(-873, 159.8) * mm});
            skLineSegment(sketch, "E416.MirrorCS", {"start": v(-823, -3.4) * mm, "end": v(-823, 46.6) * mm});
            skLineSegment(sketch, "E417.MirrorCS", {"start": v(-816.4, 24.9) * mm, "end": v(-816.4, 74.9) * mm});
            skLineSegment(sketch, "E418.MirrorCS", {"start": v(-816.4, 81.5) * mm, "end": v(-766.4, 81.5) * mm});
            skLineSegment(sketch, "E419.MirrorCS", {"start": v(-873, 166.4) * mm, "end": v(-823, 166.4) * mm});
            skLineSegment(sketch, "E420.MirrorCS", {"start": v(-873, 216.4) * mm, "end": v(-823, 216.4) * mm});
            skLineSegment(sketch, "E421.MirrorCS", {"start": v(-816.4, 131.5) * mm, "end": v(-766.4, 131.5) * mm});
            skLineSegment(sketch, "E422.MirrorCS", {"start": v(-929.6, 194.7) * mm, "end": v(-929.6, 219.7) * mm});
            skLineSegment(sketch, "E423.MirrorCS", {"start": v(-873, -60) * mm, "end": v(-823, -60) * mm});
            skLineSegment(sketch, "E424.MirrorCS", {"start": v(-823, 109.8) * mm, "end": v(-823, 159.8) * mm});
            skLineSegment(sketch, "E425.MirrorCS", {"start": v(-873, -3.4) * mm, "end": v(-823, -3.4) * mm});
            skLineSegment(sketch, "E426.MirrorCS", {"start": v(-873, -10) * mm, "end": v(-823, -10) * mm});
            skLineSegment(sketch, "E427.MirrorCS", {"start": v(-759.8, 46.6) * mm, "end": v(-709.8, 46.6) * mm});
            skLineSegment(sketch, "E428.MirrorCS", {"start": v(-759.8, 166.4) * mm, "end": v(-759.8, 216.4) * mm});
            skLineSegment(sketch, "E429.MirrorCS", {"start": v(-709.8, 53.2) * mm, "end": v(-709.8, 103.2) * mm});
            skLineSegment(sketch, "E430.MirrorCS", {"start": v(-929.6, 188.1) * mm, "end": v(-879.6, 188.1) * mm});
            skLineSegment(sketch, "E431.MirrorCS", {"start": v(-759.8, 159.8) * mm, "end": v(-709.8, 159.8) * mm});
            skLineSegment(sketch, "E432.MirrorCS", {"start": v(-873, -3.4) * mm, "end": v(-873, 46.6) * mm});
            skLineSegment(sketch, "E433.MirrorCS", {"start": v(-816.4, 219.7) * mm, "end": v(-766.4, 219.7) * mm});
            skLineSegment(sketch, "E434.MirrorCS", {"start": v(-816.4, 138.1) * mm, "end": v(-816.4, 188.1) * mm});
            skLineSegment(sketch, "E435.MirrorCS", {"start": v(-759.8, 53.2) * mm, "end": v(-759.8, 103.2) * mm});
            skLineSegment(sketch, "E436.MirrorCS", {"start": v(-816.4, -63.3) * mm, "end": v(-816.4, -38.3) * mm});
            skLineSegment(sketch, "E437.MirrorCS", {"start": v(-816.4, -38.3) * mm, "end": v(-766.4, -38.3) * mm});
            skLineSegment(sketch, "E438.MirrorCS", {"start": v(-766.4, 138.1) * mm, "end": v(-766.4, 188.1) * mm});
            skLineSegment(sketch, "E439.MirrorCS", {"start": v(-766.4, 24.9) * mm, "end": v(-766.4, 74.9) * mm});
            skLineSegment(sketch, "E440.MirrorCS", {"start": v(-709.8, -60) * mm, "end": v(-709.8, -10) * mm});
            skLineSegment(sketch, "E441.MirrorCS", {"start": v(-873, 103.2) * mm, "end": v(-823, 103.2) * mm});
            skLineSegment(sketch, "E442.MirrorCS", {"start": v(-816.4, 18.3) * mm, "end": v(-766.4, 18.3) * mm});
            skLineSegment(sketch, "E443.MirrorCS", {"start": v(-879.6, 194.7) * mm, "end": v(-879.6, 219.7) * mm});
            skLineSegment(sketch, "E444.MirrorCS", {"start": v(-759.8, -3.4) * mm, "end": v(-709.8, -3.4) * mm});
            skLineSegment(sketch, "E445.MirrorCS", {"start": v(-759.8, 53.2) * mm, "end": v(-709.8, 53.2) * mm});
            skLineSegment(sketch, "E446.MirrorCS", {"start": v(-709.8, 166.4) * mm, "end": v(-709.8, 216.4) * mm});
            skLineSegment(sketch, "E447.MirrorCS", {"start": v(-759.8, -60) * mm, "end": v(-759.8, -10) * mm});
            skLineSegment(sketch, "E448.MirrorCS", {"start": v(-816.4, 138.1) * mm, "end": v(-766.4, 138.1) * mm});
            skPoint(sketch, "E449.MirrorCS.end.orphan", {"position": v(-755.9, -63.3) * mm});
            skLineSegment(sketch, "E450", {"start": v(-929.6, 219.7) * mm, "end": v(-879.6, 219.58) * mm});
            skLineSegment(sketch, "E451.bottom", {"start": v(-1863.88, 275.88) * mm, "end": v(-653.88, 275.88) * mm});
            skLineSegment(sketch, "E451.top", {"start": v(-1863.88, -390.12) * mm, "end": v(-653.88, -390.12) * mm});
            skLineSegment(sketch, "E451.left", {"start": v(-1873.88, 243.88) * mm, "end": v(-1873.88, -358.12) * mm});
            skLineSegment(sketch, "E451.right", {"start": v(-653.88, 275.88) * mm, "end": v(-653.88, -390.12) * mm});
            skPoint(sketch, "E452", {"position": v(-1873.33, -410.13) * mm});
            skPoint(sketch, "E453", {"position": v(-1964.66, -389.7) * mm});
            skLineSegment(sketch, "E454", {"start": v(-1873.88, 243.88) * mm, "end": v(-1863.88, 243.88) * mm});
            skLineSegment(sketch, "E455", {"start": v(-1863.88, 243.88) * mm, "end": v(-1863.88, 275.88) * mm});
            skLineSegment(sketch, "E456", {"start": v(-1873.88, -358.12) * mm, "end": v(-1863.88, -358.12) * mm});
            skLineSegment(sketch, "E457", {"start": v(-1863.88, -358.12) * mm, "end": v(-1863.88, -390.12) * mm});
            skPoint(sketch, "E458.orphan", {"position": v(-1873.88, -390.12) * mm});
            skSolve(sketch);
        }
        {
            var Q0;
            Q0 = qSketchRegion(id + "F0", true);
            extrude(context, id + "F1", {"entities" : qUnion([Q0]), "depth" : 25 * mm});
        }
        {
            var Q0;
            Q0 = qSketchRegion(id + "F0", true);
            extrude(context, id + "F2", {"entities" : qUnion([Q0]), "operationType" : NewBodyOperationType.ADD, "depth" : 25 * mm});
        }
    });
